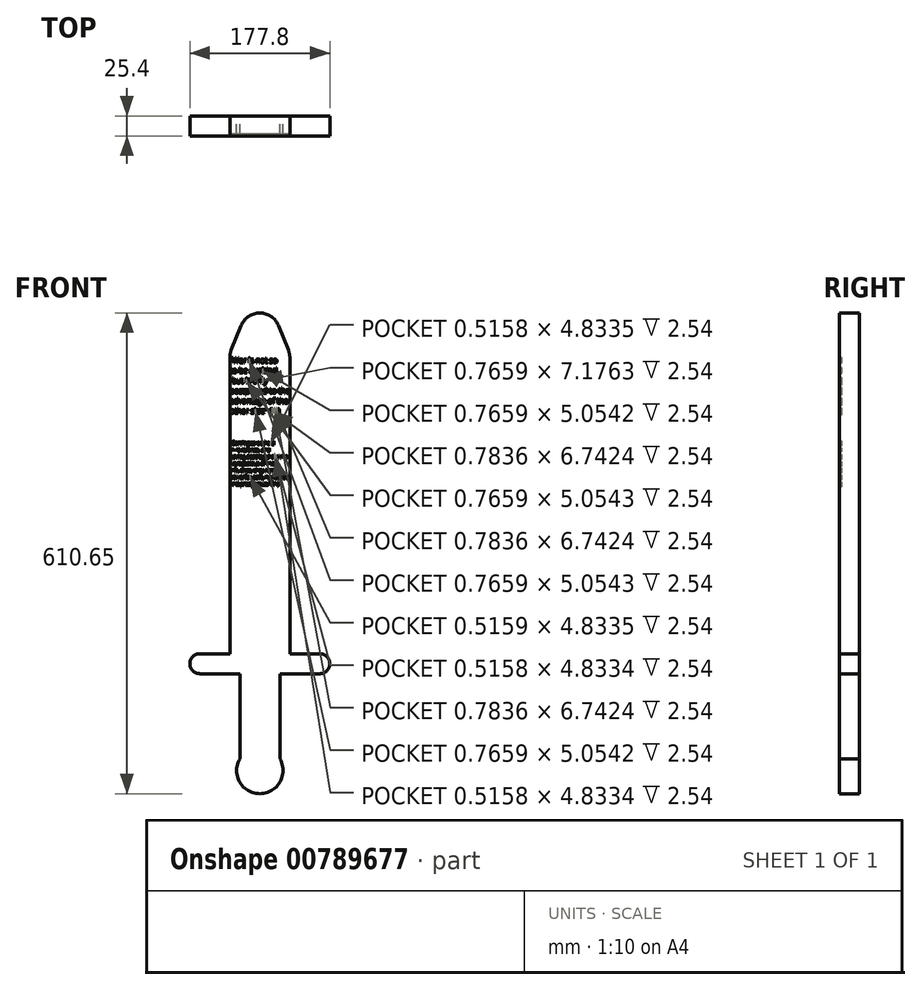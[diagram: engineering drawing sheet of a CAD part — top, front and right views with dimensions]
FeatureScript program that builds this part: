
annotation { "Feature Type Name" : "Feature", "Feature Type Description" : "" }
export const myFeature = defineFeature(function(context is Context, id is Id, definition is map)
    precondition{}
    {
        {
            var Q0;
            Q0=qCreatedBy(makeId("Front.planeOp"),FACE);
            var sketch = newSketch(context, id + "F0", { "sketchPlane" : qUnion([Q0])});
            skLineSegment(sketch, "E0", {"start": v(-25.4, -115.44) * mm, "end": v(-25.4, 36.96) * mm});
            skLineSegment(sketch, "E1", {"start": v(0, -71) * mm, "end": v(0, 36.96) * mm});
            skLineSegment(sketch, "E2", {"start": v(0, -71) * mm, "end": v(-25.4, -71) * mm, "construction": true});
            skArc(sketch, "E3", {"start": v(-25.4, -115.44) * mm, "mid": v(0.2, -100.59) * mm, "end": v(0, -71) * mm});
            skLineSegment(sketch, "E4", {"start": v(-25.4, 36.96) * mm, "end": v(0, 36.96) * mm});
            skLineSegment(sketch, "E5.MirrorCS", {"start": v(-50.8, -71) * mm, "end": v(-50.8, 36.96) * mm});
            skArc(sketch, "E6.MirrorCS", {"start": v(-25.4, -115.44) * mm, "mid": v(-51, -100.59) * mm, "end": v(-50.8, -71) * mm});
            skLineSegment(sketch, "E7.MirrorCS", {"start": v(-25.4, 36.96) * mm, "end": v(-50.8, 36.96) * mm});
            skLineSegment(sketch, "E8.bottom", {"start": v(-114.3, 36.96) * mm, "end": v(63.5, 36.96) * mm});
            skLineSegment(sketch, "E8.top", {"start": v(-114.3, 62.36) * mm, "end": v(63.5, 62.36) * mm});
            skLineSegment(sketch, "E8.left", {"start": v(-114.3, 36.96) * mm, "end": v(-114.3, 62.36) * mm});
            skLineSegment(sketch, "E8.right", {"start": v(63.5, 36.96) * mm, "end": v(63.5, 62.36) * mm});
            skLineSegment(sketch, "E9", {"start": v(-50.8, 36.96) * mm, "end": v(-50.8, 62.36) * mm, "construction": true});
            skLineSegment(sketch, "E10", {"start": v(0, 62.36) * mm, "end": v(0, 36.96) * mm, "construction": true});
            skPoint(sketch, "E11.endSnap0", {"position": v(-12.7, 36.96) * mm});
            skLineSegment(sketch, "E12", {"start": v(-25.4, 62.36) * mm, "end": v(-25.4, 36.96) * mm, "construction": true});
            skLineSegment(sketch, "E13", {"start": v(-25.4, 62.36) * mm, "end": v(-25.4, 443.36) * mm, "construction": true});
            skLineSegment(sketch, "E14", {"start": v(12.7, 62.36) * mm, "end": v(12.7, 443.36) * mm});
            skLineSegment(sketch, "E15", {"start": v(12.7, 443.36) * mm, "end": v(-63.5, 443.36) * mm});
            skLineSegment(sketch, "E16", {"start": v(-63.5, 443.36) * mm, "end": v(-63.5, 62.36) * mm});
            skLineSegment(sketch, "E17", {"start": v(-25.4, 443.36) * mm, "end": v(-25.4, 537.54) * mm, "construction": true});
            skLineSegment(sketch, "E18", {"start": v(-63.5, 443.36) * mm, "end": v(-25.4, 537.54) * mm});
            skLineSegment(sketch, "E19", {"start": v(12.7, 443.36) * mm, "end": v(-25.4, 537.54) * mm});
            skSolve(sketch);
        }
        {
            var Q0;
            {var subQ0=sQuery(id+"F0.wireOp",EDGE,"E0");Q0=makeQuery(id+"F0.imprint","IMPRINT",FACE,{"disambiguationData":[TD([[makeQuery(id+"F0.imprint","IMPRINT",EDGE,{"derivedFrom":subQ0}),1.0]])]});}
            var Q1;
            {var subQ0=sQuery(id+"F0.wireOp",EDGE,"E0");Q1=makeQuery(id+"F0.imprint","IMPRINT",FACE,{"disambiguationData":[TD([[makeQuery(id+"F0.imprint","IMPRINT",EDGE,{"derivedFrom":subQ0}),-1.0]])]});}
            var Q2;
            {var subQ5=sQuery(id+"F0.wireOp",EDGE,"E8.left");Q2=makeQuery(id+"F0.imprint","IMPRINT",FACE,{"disambiguationData":[TD([[makeQuery(id+"F0.imprint","IMPRINT",EDGE,{"derivedFrom":subQ5}),-1.0]])]});}
            var Q3;
            {var subQ0=sQuery(id+"F0.wireOp",EDGE,"k9AxdfFr-KBrS-fMyl-MdHl-o8JCi0EdSjDJ");Q3=makeQuery(id+"F0.imprint","IMPRINT",FACE,{"disambiguationData":[TD([[makeQuery(id+"F0.imprint","IMPRINT",EDGE,{"derivedFrom":subQ0}),-1.0]])]});}
            var Q4;
            {var subQ0=sQuery(id+"F0.wireOp",EDGE,"E14");Q4=makeQuery(id+"F0.imprint","IMPRINT",FACE,{"disambiguationData":[TD([[makeQuery(id+"F0.imprint","IMPRINT",EDGE,{"derivedFrom":subQ0}),1.0]])]});}
            var Q5;
            Q5=makeQuery(id+"F0.imprint","IMPRINT",FACE,{"disambiguationData":[TD([[makeQuery(id+"F0.imprint","IMPRINT",EDGE,{"derivedFrom":sQuery(id+"F0.wireOp",EDGE,"E15")}),-1.0]])]});
            var Q6;
            Q6=sQuery(id+"F0.wireOp",EDGE,"k9AxdfFr-KBrS-fMyl-MdHl-o8JCi0EdSjDJ");
            extrude(context, id + "F1", {"entities" : qUnion([Q0, Q1, Q2, Q3, Q4, Q5]), "surfaceEntities" : qUnion([Q6]), "depth" : 25.4 * mm, "offsetDistance" : 25.4 * mm});
        }
        {
            var Q0;
            Q0=makeQuery(id+"F1.opExtrude","SWEPT_EDGE",EDGE,{"disambiguationData":[OSD([sQuery(id+"F0.wireOp",EDGE,"E18"),sQuery(id+"F0.wireOp",EDGE,"E19")])]});
            var Q1;
            Q1=makeQuery(id+"F1.opExtrude","SWEPT_EDGE",EDGE,{"disambiguationData":[OSD([sQuery(id+"F0.wireOp",EDGE,"E14"),sQuery(id+"F0.wireOp",EDGE,"E15"),sQuery(id+"F0.wireOp",EDGE,"E19")])]});
            var Q2;
            Q2=makeQuery(id+"F1.opExtrude","SWEPT_EDGE",EDGE,{"disambiguationData":[OSD([sQuery(id+"F0.wireOp",EDGE,"E15"),sQuery(id+"F0.wireOp",EDGE,"E16"),sQuery(id+"F0.wireOp",EDGE,"E18")])]});
            fillet(context, id + "F2", {"entities" : qUnion([Q0, Q1, Q2]), "radius" : 25.4 * mm, "tangentPropagation" : true, "allowEdgeOverflow" : false});
        }
        {
            var Q0;
            Q0=makeQuery(id+"F1.opExtrude","SWEPT_EDGE",EDGE,{"disambiguationData":[OSD([sQuery(id+"F0.wireOp",EDGE,"E8.top"),sQuery(id+"F0.wireOp",EDGE,"E8.left")])]});
            var Q1;
            Q1=makeQuery(id+"F1.opExtrude","SWEPT_EDGE",EDGE,{"disambiguationData":[OSD([sQuery(id+"F0.wireOp",EDGE,"E8.bottom"),sQuery(id+"F0.wireOp",EDGE,"E8.left")])]});
            var Q2;
            Q2=makeQuery(id+"F1.opExtrude","SWEPT_EDGE",EDGE,{"disambiguationData":[OSD([sQuery(id+"F0.wireOp",EDGE,"E8.top"),sQuery(id+"F0.wireOp",EDGE,"E8.right")])]});
            var Q3;
            Q3=makeQuery(id+"F1.opExtrude","SWEPT_EDGE",EDGE,{"disambiguationData":[OSD([sQuery(id+"F0.wireOp",EDGE,"E8.bottom"),sQuery(id+"F0.wireOp",EDGE,"E8.right")])]});
            fillet(context, id + "F3", {"entities" : qUnion([Q0, Q1, Q2, Q3]), "radius" : 12.7 * mm, "tangentPropagation" : true, "allowEdgeOverflow" : false});
        }
        {
            var Q0;
            Q0=makeQuery(id+"F1.opExtrude","CAP_FACE",FACE,{"disambiguationData":[OSD([sQuery(id+"F0.wireOp",EDGE,"E1"),sQuery(id+"F0.wireOp",EDGE,"E3"),sQuery(id+"F0.wireOp",EDGE,"E5.MirrorCS"),sQuery(id+"F0.wireOp",EDGE,"E6.MirrorCS"),sQuery(id+"F0.wireOp",EDGE,"E8.bottom"),sQuery(id+"F0.wireOp",EDGE,"E8.top"),sQuery(id+"F0.wireOp",EDGE,"E8.left"),sQuery(id+"F0.wireOp",EDGE,"E8.right"),sQuery(id+"F0.wireOp",EDGE,"E14"),sQuery(id+"F0.wireOp",EDGE,"E16"),sQuery(id+"F0.wireOp",EDGE,"E18"),sQuery(id+"F0.wireOp",EDGE,"E19")])],"isStart":false});
            var sketch = newSketch(context, id + "F4", { "sketchPlane" : qUnion([Q0])});
            skText(sketch, "E20", { "text": "“War is not so \nto be avoided,\n but is only \npostponed to the \nadvantage of the \nother side” (III)", "fontName": "OpenSans-Regular.ttf"});
            skText(sketch, "E21", { "text": "“Coming to be held \nin reverence, and \nhaving destroyed all who \nwere jealous of their \ninfluence, they remain \npowerful, safe, honoured, \nand prosperous.” (VI)", "fontName": "OpenSans-Regular.ttf"});
            const initialGuessF4  = {"E20": [-0.0635, 0.43161, 1, 0, 0.0068], "E21": [-0.0635, 0.32779, 1, 0, 0.00458]};
            skSetInitialGuess(sketch, initialGuessF4);
            skSolve(sketch);
        }
        {
            var Q0;
            Q0=makeQuery(id+"F4.imprint","IMPRINT",FACE,{"disambiguationData":[TD([[makeQuery(id+"F4.imprint","IMPRINT",EDGE,{"derivedFrom":sQuery(id+"F4.wireOp",EDGE,"E20.sketch_text.stroke-614")}),-1.0]])]});
            var Q1;
            Q1=makeQuery(id+"F4.imprint","IMPRINT",FACE,{"disambiguationData":[TD([[makeQuery(id+"F4.imprint","IMPRINT",EDGE,{"derivedFrom":sQuery(id+"F4.wireOp",EDGE,"E20.sketch_text.stroke-363")}),1.0]])]});
            var Q2;
            Q2=makeQuery(id+"F4.imprint","IMPRINT",FACE,{"disambiguationData":[TD([[makeQuery(id+"F4.imprint","IMPRINT",EDGE,{"derivedFrom":sQuery(id+"F4.wireOp",EDGE,"E21.sketch_text.stroke-2180")}),1.0]])]});
            var Q3;
            Q3=makeQuery(id+"F4.imprint","IMPRINT",FACE,{"disambiguationData":[TD([[makeQuery(id+"F4.imprint","IMPRINT",EDGE,{"derivedFrom":sQuery(id+"F4.wireOp",EDGE,"E21.sketch_text.stroke-1878")}),1.0]])]});
            var Q4;
            Q4=makeQuery(id+"F4.imprint","IMPRINT",FACE,{"disambiguationData":[TD([[makeQuery(id+"F4.imprint","IMPRINT",EDGE,{"derivedFrom":sQuery(id+"F4.wireOp",EDGE,"E21.sketch_text.stroke-1614")}),1.0]])]});
            var Q5;
            Q5=makeQuery(id+"F4.imprint","IMPRINT",FACE,{"disambiguationData":[TD([[makeQuery(id+"F4.imprint","IMPRINT",EDGE,{"derivedFrom":sQuery(id+"F4.wireOp",EDGE,"E21.sketch_text.stroke-1142")}),1.0]])]});
            var Q6;
            Q6=makeQuery(id+"F4.imprint","IMPRINT",FACE,{"disambiguationData":[TD([[makeQuery(id+"F4.imprint","IMPRINT",EDGE,{"derivedFrom":sQuery(id+"F4.wireOp",EDGE,"E20.sketch_text.stroke-674")}),1.0]])]});
            var Q7;
            Q7=makeQuery(id+"F4.imprint","IMPRINT",FACE,{"disambiguationData":[TD([[makeQuery(id+"F4.imprint","IMPRINT",EDGE,{"derivedFrom":sQuery(id+"F4.wireOp",EDGE,"E20.sketch_text.stroke-406")}),1.0]])]});
            var Q8;
            Q8=makeQuery(id+"F4.imprint","IMPRINT",FACE,{"disambiguationData":[TD([[makeQuery(id+"F4.imprint","IMPRINT",EDGE,{"derivedFrom":sQuery(id+"F4.wireOp",EDGE,"E20.sketch_text.stroke-995")}),1.0]])]});
            var Q9;
            Q9=makeQuery(id+"F4.imprint","IMPRINT",FACE,{"disambiguationData":[TD([[makeQuery(id+"F4.imprint","IMPRINT",EDGE,{"derivedFrom":sQuery(id+"F4.wireOp",EDGE,"E20.sketch_text.stroke-692")}),1.0]])]});
            var Q10;
            Q10=makeQuery(id+"F4.imprint","IMPRINT",FACE,{"disambiguationData":[TD([[makeQuery(id+"F4.imprint","IMPRINT",EDGE,{"derivedFrom":sQuery(id+"F4.wireOp",EDGE,"E20.sketch_text.stroke-1294")}),1.0]])]});
            var Q11;
            Q11=makeQuery(id+"F4.imprint","IMPRINT",FACE,{"disambiguationData":[TD([[makeQuery(id+"F4.imprint","IMPRINT",EDGE,{"derivedFrom":sQuery(id+"F4.wireOp",EDGE,"E20.sketch_text.stroke-1032")}),1.0]])]});
            var Q12;
            Q12=makeQuery(id+"F4.imprint","IMPRINT",FACE,{"disambiguationData":[TD([[makeQuery(id+"F4.imprint","IMPRINT",EDGE,{"derivedFrom":sQuery(id+"F4.wireOp",EDGE,"E20.sketch_text.stroke-437")}),1.0]])]});
            var Q13;
            Q13=makeQuery(id+"F4.imprint","IMPRINT",FACE,{"disambiguationData":[TD([[makeQuery(id+"F4.imprint","IMPRINT",EDGE,{"derivedFrom":sQuery(id+"F4.wireOp",EDGE,"E20.sketch_text.stroke-1041")}),1.0]])]});
            var Q14;
            Q14=makeQuery(id+"F4.imprint","IMPRINT",FACE,{"disambiguationData":[TD([[makeQuery(id+"F4.imprint","IMPRINT",EDGE,{"derivedFrom":sQuery(id+"F4.wireOp",EDGE,"E21.sketch_text.stroke-925")}),1.0]])]});
            var Q15;
            Q15=makeQuery(id+"F4.imprint","IMPRINT",FACE,{"disambiguationData":[TD([[makeQuery(id+"F4.imprint","IMPRINT",EDGE,{"derivedFrom":sQuery(id+"F4.wireOp",EDGE,"E21.sketch_text.stroke-649")}),1.0]])]});
            var Q16;
            Q16=makeQuery(id+"F4.imprint","IMPRINT",FACE,{"disambiguationData":[TD([[makeQuery(id+"F4.imprint","IMPRINT",EDGE,{"derivedFrom":sQuery(id+"F4.wireOp",EDGE,"E21.sketch_text.stroke-1950")}),1.0]])]});
            var Q17;
            Q17=makeQuery(id+"F4.imprint","IMPRINT",FACE,{"disambiguationData":[TD([[makeQuery(id+"F4.imprint","IMPRINT",EDGE,{"derivedFrom":sQuery(id+"F4.wireOp",EDGE,"E20.sketch_text.stroke-731")}),1.0]])]});
            var Q18;
            Q18=makeQuery(id+"F4.imprint","IMPRINT",FACE,{"disambiguationData":[TD([[makeQuery(id+"F4.imprint","IMPRINT",EDGE,{"derivedFrom":sQuery(id+"F4.wireOp",EDGE,"E21.sketch_text.stroke-139")}),1.0]])]});
            var Q19;
            Q19=makeQuery(id+"F4.imprint","IMPRINT",FACE,{"disambiguationData":[TD([[makeQuery(id+"F4.imprint","IMPRINT",EDGE,{"derivedFrom":sQuery(id+"F4.wireOp",EDGE,"E20.sketch_text.stroke-422")}),-1.0]])]});
            var Q20;
            Q20=makeQuery(id+"F4.imprint","IMPRINT",FACE,{"disambiguationData":[TD([[makeQuery(id+"F4.imprint","IMPRINT",EDGE,{"derivedFrom":sQuery(id+"F4.wireOp",EDGE,"E20.sketch_text.stroke-751")}),1.0]])]});
            var Q21;
            Q21=makeQuery(id+"F4.imprint","IMPRINT",FACE,{"disambiguationData":[TD([[makeQuery(id+"F4.imprint","IMPRINT",EDGE,{"derivedFrom":sQuery(id+"F4.wireOp",EDGE,"E20.sketch_text.stroke-1075")}),1.0]])]});
            var Q22;
            Q22=makeQuery(id+"F4.imprint","IMPRINT",FACE,{"disambiguationData":[TD([[makeQuery(id+"F4.imprint","IMPRINT",EDGE,{"derivedFrom":sQuery(id+"F4.wireOp",EDGE,"E21.sketch_text.stroke-679")}),1.0]])]});
            var Q23;
            Q23=makeQuery(id+"F4.imprint","IMPRINT",FACE,{"disambiguationData":[TD([[makeQuery(id+"F4.imprint","IMPRINT",EDGE,{"derivedFrom":sQuery(id+"F4.wireOp",EDGE,"E20.sketch_text.stroke-518")}),-1.0]])]});
            var Q24;
            Q24=makeQuery(id+"F4.imprint","IMPRINT",FACE,{"disambiguationData":[TD([[makeQuery(id+"F4.imprint","IMPRINT",EDGE,{"derivedFrom":sQuery(id+"F4.wireOp",EDGE,"E20.sketch_text.stroke-1156")}),-1.0]])]});
            var Q25;
            Q25=makeQuery(id+"F4.imprint","IMPRINT",FACE,{"disambiguationData":[TD([[makeQuery(id+"F4.imprint","IMPRINT",EDGE,{"derivedFrom":sQuery(id+"F4.wireOp",EDGE,"E20.sketch_text.stroke-255")}),1.0]])]});
            var Q26;
            Q26=makeQuery(id+"F4.imprint","IMPRINT",FACE,{"disambiguationData":[TD([[makeQuery(id+"F4.imprint","IMPRINT",EDGE,{"derivedFrom":sQuery(id+"F4.wireOp",EDGE,"E20.sketch_text.stroke-232")}),1.0]])]});
            var Q27;
            Q27=makeQuery(id+"F4.imprint","IMPRINT",FACE,{"disambiguationData":[TD([[makeQuery(id+"F4.imprint","IMPRINT",EDGE,{"derivedFrom":sQuery(id+"F4.wireOp",EDGE,"E20.sketch_text.stroke-51")}),1.0]])]});
            var Q28;
            Q28=makeQuery(id+"F4.imprint","IMPRINT",FACE,{"disambiguationData":[TD([[makeQuery(id+"F4.imprint","IMPRINT",EDGE,{"derivedFrom":sQuery(id+"F4.wireOp",EDGE,"E20.sketch_text.stroke-135")}),1.0]])]});
            var Q29;
            Q29=makeQuery(id+"F4.imprint","IMPRINT",FACE,{"disambiguationData":[TD([[makeQuery(id+"F4.imprint","IMPRINT",EDGE,{"derivedFrom":sQuery(id+"F4.wireOp",EDGE,"E20.sketch_text.stroke-196")}),1.0]])]});
            var Q30;
            Q30=makeQuery(id+"F4.imprint","IMPRINT",FACE,{"disambiguationData":[TD([[makeQuery(id+"F4.imprint","IMPRINT",EDGE,{"derivedFrom":sQuery(id+"F4.wireOp",EDGE,"E21.sketch_text.stroke-2050")}),1.0]])]});
            var Q31;
            Q31=makeQuery(id+"F4.imprint","IMPRINT",FACE,{"disambiguationData":[TD([[makeQuery(id+"F4.imprint","IMPRINT",EDGE,{"derivedFrom":sQuery(id+"F4.wireOp",EDGE,"E21.sketch_text.stroke-173")}),1.0]])]});
            var Q32;
            Q32=makeQuery(id+"F4.imprint","IMPRINT",FACE,{"disambiguationData":[TD([[makeQuery(id+"F4.imprint","IMPRINT",EDGE,{"derivedFrom":sQuery(id+"F4.wireOp",EDGE,"E20.sketch_text.stroke-1335")}),-1.0]])]});
            var Q33;
            Q33=makeQuery(id+"F4.imprint","IMPRINT",FACE,{"disambiguationData":[TD([[makeQuery(id+"F4.imprint","IMPRINT",EDGE,{"derivedFrom":sQuery(id+"F4.wireOp",EDGE,"E20.sketch_text.stroke-788")}),1.0]])]});
            var Q34;
            Q34=makeQuery(id+"F4.imprint","IMPRINT",FACE,{"disambiguationData":[TD([[makeQuery(id+"F4.imprint","IMPRINT",EDGE,{"derivedFrom":sQuery(id+"F4.wireOp",EDGE,"E21.sketch_text.stroke-196")}),1.0]])]});
            var Q35;
            Q35=makeQuery(id+"F4.imprint","IMPRINT",FACE,{"disambiguationData":[TD([[makeQuery(id+"F4.imprint","IMPRINT",EDGE,{"derivedFrom":sQuery(id+"F4.wireOp",EDGE,"E21.sketch_text.stroke-2025")}),1.0]])]});
            var Q36;
            Q36=makeQuery(id+"F4.imprint","IMPRINT",FACE,{"disambiguationData":[TD([[makeQuery(id+"F4.imprint","IMPRINT",EDGE,{"derivedFrom":sQuery(id+"F4.wireOp",EDGE,"E20.sketch_text.stroke-527")}),1.0]])]});
            var Q37;
            Q37=makeQuery(id+"F4.imprint","IMPRINT",FACE,{"disambiguationData":[TD([[makeQuery(id+"F4.imprint","IMPRINT",EDGE,{"derivedFrom":sQuery(id+"F4.wireOp",EDGE,"E20.sketch_text.stroke-1165")}),1.0]])]});
            var Q38;
            Q38=makeQuery(id+"F4.imprint","IMPRINT",FACE,{"disambiguationData":[TD([[makeQuery(id+"F4.imprint","IMPRINT",EDGE,{"derivedFrom":sQuery(id+"F4.wireOp",EDGE,"E20.sketch_text.stroke-847")}),1.0]])]});
            var Q39;
            Q39=makeQuery(id+"F4.imprint","IMPRINT",FACE,{"disambiguationData":[TD([[makeQuery(id+"F4.imprint","IMPRINT",EDGE,{"derivedFrom":sQuery(id+"F4.wireOp",EDGE,"E20.sketch_text.stroke-301")}),1.0]])]});
            var Q40;
            Q40=makeQuery(id+"F4.imprint","IMPRINT",FACE,{"disambiguationData":[TD([[makeQuery(id+"F4.imprint","IMPRINT",EDGE,{"derivedFrom":sQuery(id+"F4.wireOp",EDGE,"E21.sketch_text.stroke-773")}),1.0]])]});
            var Q41;
            Q41=makeQuery(id+"F4.imprint","IMPRINT",FACE,{"disambiguationData":[TD([[makeQuery(id+"F4.imprint","IMPRINT",EDGE,{"derivedFrom":sQuery(id+"F4.wireOp",EDGE,"E21.sketch_text.stroke-2081")}),1.0]])]});
            var Q42;
            Q42=makeQuery(id+"F4.imprint","IMPRINT",FACE,{"disambiguationData":[TD([[makeQuery(id+"F4.imprint","IMPRINT",EDGE,{"derivedFrom":sQuery(id+"F4.wireOp",EDGE,"E20.sketch_text.stroke-871")}),1.0]])]});
            var Q43;
            Q43=makeQuery(id+"F4.imprint","IMPRINT",FACE,{"disambiguationData":[TD([[makeQuery(id+"F4.imprint","IMPRINT",EDGE,{"derivedFrom":sQuery(id+"F4.wireOp",EDGE,"E21.sketch_text.stroke-1062")}),1.0]])]});
            var Q44;
            Q44=makeQuery(id+"F4.imprint","IMPRINT",FACE,{"disambiguationData":[TD([[makeQuery(id+"F4.imprint","IMPRINT",EDGE,{"derivedFrom":sQuery(id+"F4.wireOp",EDGE,"E20.sketch_text.stroke-1192")}),-1.0]])]});
            var Q45;
            Q45=makeQuery(id+"F4.imprint","IMPRINT",FACE,{"disambiguationData":[TD([[makeQuery(id+"F4.imprint","IMPRINT",EDGE,{"derivedFrom":sQuery(id+"F4.wireOp",EDGE,"E20.sketch_text.stroke-894")}),1.0]])]});
            var Q46;
            Q46=makeQuery(id+"F4.imprint","IMPRINT",FACE,{"disambiguationData":[TD([[makeQuery(id+"F4.imprint","IMPRINT",EDGE,{"derivedFrom":sQuery(id+"F4.wireOp",EDGE,"E20.sketch_text.stroke-328")}),1.0]])]});
            var Q47;
            Q47=makeQuery(id+"F4.imprint","IMPRINT",FACE,{"disambiguationData":[TD([[makeQuery(id+"F4.imprint","IMPRINT",EDGE,{"derivedFrom":sQuery(id+"F4.wireOp",EDGE,"E21.sketch_text.stroke-527")}),1.0]])]});
            var Q48;
            Q48=makeQuery(id+"F4.imprint","IMPRINT",FACE,{"disambiguationData":[TD([[makeQuery(id+"F4.imprint","IMPRINT",EDGE,{"derivedFrom":sQuery(id+"F4.wireOp",EDGE,"E21.sketch_text.stroke-279")}),1.0]])]});
            var Q49;
            Q49=makeQuery(id+"F4.imprint","IMPRINT",FACE,{"disambiguationData":[TD([[makeQuery(id+"F4.imprint","IMPRINT",EDGE,{"derivedFrom":sQuery(id+"F4.wireOp",EDGE,"E21.sketch_text.stroke-2130")}),1.0]])]});
            var Q50;
            Q50=makeQuery(id+"F4.imprint","IMPRINT",FACE,{"disambiguationData":[TD([[makeQuery(id+"F4.imprint","IMPRINT",EDGE,{"derivedFrom":sQuery(id+"F4.wireOp",EDGE,"E20.sketch_text.stroke-1224")}),1.0]])]});
            var Q51;
            Q51=makeQuery(id+"F4.imprint","IMPRINT",FACE,{"disambiguationData":[TD([[makeQuery(id+"F4.imprint","IMPRINT",EDGE,{"derivedFrom":sQuery(id+"F4.wireOp",EDGE,"E20.sketch_text.stroke-588")}),1.0]])]});
            var Q52;
            Q52=makeQuery(id+"F4.imprint","IMPRINT",FACE,{"disambiguationData":[TD([[makeQuery(id+"F4.imprint","IMPRINT",EDGE,{"derivedFrom":sQuery(id+"F4.wireOp",EDGE,"E21.sketch_text.stroke-831")}),1.0]])]});
            var Q53;
            Q53=makeQuery(id+"F4.imprint","IMPRINT",FACE,{"disambiguationData":[TD([[makeQuery(id+"F4.imprint","IMPRINT",EDGE,{"derivedFrom":sQuery(id+"F4.wireOp",EDGE,"E21.sketch_text.stroke-1844")}),1.0]])]});
            var Q54;
            Q54=makeQuery(id+"F4.imprint","IMPRINT",FACE,{"disambiguationData":[TD([[makeQuery(id+"F4.imprint","IMPRINT",EDGE,{"derivedFrom":sQuery(id+"F4.wireOp",EDGE,"E21.sketch_text.stroke-1083")}),1.0]])]});
            var Q55;
            Q55=makeQuery(id+"F4.imprint","IMPRINT",FACE,{"disambiguationData":[TD([[makeQuery(id+"F4.imprint","IMPRINT",EDGE,{"derivedFrom":sQuery(id+"F4.wireOp",EDGE,"E20.sketch_text.stroke-932")}),1.0]])]});
            var Q56;
            Q56=makeQuery(id+"F4.imprint","IMPRINT",FACE,{"disambiguationData":[TD([[makeQuery(id+"F4.imprint","IMPRINT",EDGE,{"derivedFrom":sQuery(id+"F4.wireOp",EDGE,"E20.sketch_text.stroke-606")}),1.0]])]});
            var Q57;
            Q57=makeQuery(id+"F4.imprint","IMPRINT",FACE,{"disambiguationData":[TD([[makeQuery(id+"F4.imprint","IMPRINT",EDGE,{"derivedFrom":sQuery(id+"F4.wireOp",EDGE,"E21.sketch_text.stroke-36")}),1.0]])]});
            var Q58;
            Q58=makeQuery(id+"F4.imprint","IMPRINT",FACE,{"disambiguationData":[TD([[makeQuery(id+"F4.imprint","IMPRINT",EDGE,{"derivedFrom":sQuery(id+"F4.wireOp",EDGE,"E21.sketch_text.stroke-1596")}),1.0]])]});
            var Q59;
            Q59=makeQuery(id+"F4.imprint","IMPRINT",FACE,{"disambiguationData":[TD([[makeQuery(id+"F4.imprint","IMPRINT",EDGE,{"derivedFrom":sQuery(id+"F4.wireOp",EDGE,"E21.sketch_text.stroke-300")}),-1.0]])]});
            var Q60;
            Q60=makeQuery(id+"F4.imprint","IMPRINT",FACE,{"disambiguationData":[TD([[makeQuery(id+"F4.imprint","IMPRINT",EDGE,{"derivedFrom":sQuery(id+"F4.wireOp",EDGE,"E21.sketch_text.stroke-44")}),-1.0]])]});
            var Q61;
            Q61=makeQuery(id+"F4.imprint","IMPRINT",FACE,{"disambiguationData":[TD([[makeQuery(id+"F4.imprint","IMPRINT",EDGE,{"derivedFrom":sQuery(id+"F4.wireOp",EDGE,"E20.sketch_text.stroke-1242")}),-1.0]])]});
            var Q62;
            Q62=makeQuery(id+"F4.imprint","IMPRINT",FACE,{"disambiguationData":[TD([[makeQuery(id+"F4.imprint","IMPRINT",EDGE,{"derivedFrom":sQuery(id+"F4.wireOp",EDGE,"E20.sketch_text.stroke-940")}),-1.0]])]});
            var Q63;
            Q63=makeQuery(id+"F4.imprint","IMPRINT",FACE,{"disambiguationData":[TD([[makeQuery(id+"F4.imprint","IMPRINT",EDGE,{"derivedFrom":sQuery(id+"F4.wireOp",EDGE,"E21.sketch_text.stroke-1334")}),-1.0]])]});
            var Q64;
            Q64=makeQuery(id+"F4.imprint","IMPRINT",FACE,{"disambiguationData":[TD([[makeQuery(id+"F4.imprint","IMPRINT",EDGE,{"derivedFrom":sQuery(id+"F4.wireOp",EDGE,"E21.sketch_text.stroke-1108")}),-1.0]])]});
            var Q65;
            Q65=makeQuery(id+"F4.imprint","IMPRINT",FACE,{"disambiguationData":[TD([[makeQuery(id+"F4.imprint","IMPRINT",EDGE,{"derivedFrom":sQuery(id+"F4.wireOp",EDGE,"E21.sketch_text.stroke-867")}),-1.0]])]});
            var Q66;
            Q66=makeQuery(id+"F4.imprint","IMPRINT",FACE,{"disambiguationData":[TD([[makeQuery(id+"F4.imprint","IMPRINT",EDGE,{"derivedFrom":sQuery(id+"F4.wireOp",EDGE,"E21.sketch_text.stroke-581")}),-1.0]])]});
            var Q67;
            Q67=makeQuery(id+"F4.imprint","IMPRINT",FACE,{"disambiguationData":[TD([[makeQuery(id+"F4.imprint","IMPRINT",EDGE,{"derivedFrom":sQuery(id+"F4.wireOp",EDGE,"E20.sketch_text.stroke-282")}),-1.0]])]});
            var Q68;
            Q68=makeQuery(id+"F4.imprint","IMPRINT",FACE,{"disambiguationData":[TD([[makeQuery(id+"F4.imprint","IMPRINT",EDGE,{"derivedFrom":sQuery(id+"F4.wireOp",EDGE,"E21.sketch_text.stroke-1869")}),-1.0]])]});
            var Q69;
            Q69=makeQuery(id+"F4.imprint","IMPRINT",FACE,{"disambiguationData":[TD([[makeQuery(id+"F4.imprint","IMPRINT",EDGE,{"derivedFrom":sQuery(id+"F4.wireOp",EDGE,"E21.sketch_text.stroke-1024")}),-1.0]])]});
            var Q70;
            Q70=makeQuery(id+"F4.imprint","IMPRINT",FACE,{"disambiguationData":[TD([[makeQuery(id+"F4.imprint","IMPRINT",EDGE,{"derivedFrom":sQuery(id+"F4.wireOp",EDGE,"E21.sketch_text.stroke-330")}),-1.0]])]});
            var Q71;
            Q71=makeQuery(id+"F4.imprint","IMPRINT",FACE,{"disambiguationData":[TD([[makeQuery(id+"F4.imprint","IMPRINT",EDGE,{"derivedFrom":sQuery(id+"F4.wireOp",EDGE,"E20.sketch_text.stroke-879")}),-1.0]])]});
            var Q72;
            Q72=makeQuery(id+"F4.imprint","IMPRINT",FACE,{"disambiguationData":[TD([[makeQuery(id+"F4.imprint","IMPRINT",EDGE,{"derivedFrom":sQuery(id+"F4.wireOp",EDGE,"E20.sketch_text.stroke-1267")}),-1.0]])]});
            var Q73;
            Q73=makeQuery(id+"F4.imprint","IMPRINT",FACE,{"disambiguationData":[TD([[makeQuery(id+"F4.imprint","IMPRINT",EDGE,{"derivedFrom":sQuery(id+"F4.wireOp",EDGE,"E20.sketch_text.stroke-957")}),-1.0]])]});
            var Q74;
            Q74=makeQuery(id+"F4.imprint","IMPRINT",FACE,{"disambiguationData":[TD([[makeQuery(id+"F4.imprint","IMPRINT",EDGE,{"derivedFrom":sQuery(id+"F4.wireOp",EDGE,"E21.sketch_text.stroke-1351")}),-1.0]])]});
            var Q75;
            Q75=makeQuery(id+"F4.imprint","IMPRINT",FACE,{"disambiguationData":[TD([[makeQuery(id+"F4.imprint","IMPRINT",EDGE,{"derivedFrom":sQuery(id+"F4.wireOp",EDGE,"E21.sketch_text.stroke-871")}),-1.0]])]});
            var Q76;
            Q76=makeQuery(id+"F4.imprint","IMPRINT",FACE,{"disambiguationData":[TD([[makeQuery(id+"F4.imprint","IMPRINT",EDGE,{"derivedFrom":sQuery(id+"F4.wireOp",EDGE,"E21.sketch_text.stroke-591")}),-1.0]])]});
            var Q77;
            Q77=makeQuery(id+"F4.imprint","IMPRINT",FACE,{"disambiguationData":[TD([[makeQuery(id+"F4.imprint","IMPRINT",EDGE,{"derivedFrom":sQuery(id+"F4.wireOp",EDGE,"E20.sketch_text.stroke-319")}),-1.0]])]});
            var Q78;
            Q78=makeQuery(id+"F4.imprint","IMPRINT",FACE,{"disambiguationData":[TD([[makeQuery(id+"F4.imprint","IMPRINT",EDGE,{"derivedFrom":sQuery(id+"F4.wireOp",EDGE,"E21.sketch_text.stroke-2188")}),-1.0]])]});
            var Q79;
            Q79=makeQuery(id+"F4.imprint","IMPRINT",FACE,{"disambiguationData":[TD([[makeQuery(id+"F4.imprint","IMPRINT",EDGE,{"derivedFrom":sQuery(id+"F4.wireOp",EDGE,"E21.sketch_text.stroke-1886")}),-1.0]])]});
            var Q80;
            Q80=makeQuery(id+"F4.imprint","IMPRINT",FACE,{"disambiguationData":[TD([[makeQuery(id+"F4.imprint","IMPRINT",EDGE,{"derivedFrom":sQuery(id+"F4.wireOp",EDGE,"E21.sketch_text.stroke-1622")}),-1.0]])]});
            var Q81;
            Q81=makeQuery(id+"F4.imprint","IMPRINT",FACE,{"disambiguationData":[TD([[makeQuery(id+"F4.imprint","IMPRINT",EDGE,{"derivedFrom":sQuery(id+"F4.wireOp",EDGE,"E21.sketch_text.stroke-1916")}),-1.0]])]});
            var Q82;
            Q82=makeQuery(id+"F4.imprint","IMPRINT",FACE,{"disambiguationData":[TD([[makeQuery(id+"F4.imprint","IMPRINT",EDGE,{"derivedFrom":sQuery(id+"F4.wireOp",EDGE,"E21.sketch_text.stroke-1043")}),-1.0]])]});
            var Q83;
            Q83=makeQuery(id+"F4.imprint","IMPRINT",FACE,{"disambiguationData":[TD([[makeQuery(id+"F4.imprint","IMPRINT",EDGE,{"derivedFrom":sQuery(id+"F4.wireOp",EDGE,"E21.sketch_text.stroke-359")}),-1.0]])]});
            var Q84;
            Q84=makeQuery(id+"F4.imprint","IMPRINT",FACE,{"disambiguationData":[TD([[makeQuery(id+"F4.imprint","IMPRINT",EDGE,{"derivedFrom":sQuery(id+"F4.wireOp",EDGE,"E20.sketch_text.stroke-913")}),-1.0]])]});
            var Q85;
            Q85=makeQuery(id+"F4.imprint","IMPRINT",FACE,{"disambiguationData":[TD([[makeQuery(id+"F4.imprint","IMPRINT",EDGE,{"derivedFrom":sQuery(id+"F4.wireOp",EDGE,"E20.sketch_text.stroke-639")}),-1.0]])]});
            var Q86;
            Q86=makeQuery(id+"F4.imprint","IMPRINT",FACE,{"disambiguationData":[TD([[makeQuery(id+"F4.imprint","IMPRINT",EDGE,{"derivedFrom":sQuery(id+"F4.wireOp",EDGE,"E20.sketch_text.stroke-386")}),1.0]])]});
            var Q87;
            Q87=makeQuery(id+"F4.imprint","IMPRINT",FACE,{"disambiguationData":[TD([[makeQuery(id+"F4.imprint","IMPRINT",EDGE,{"derivedFrom":sQuery(id+"F4.wireOp",EDGE,"E21.sketch_text.stroke-1150")}),-1.0]])]});
            var Q88;
            Q88=makeQuery(id+"F4.imprint","IMPRINT",FACE,{"disambiguationData":[TD([[makeQuery(id+"F4.imprint","IMPRINT",EDGE,{"derivedFrom":sQuery(id+"F4.wireOp",EDGE,"E21.sketch_text.stroke-875")}),-1.0]])]});
            var Q89;
            Q89=makeQuery(id+"F4.imprint","IMPRINT",FACE,{"disambiguationData":[TD([[makeQuery(id+"F4.imprint","IMPRINT",EDGE,{"derivedFrom":sQuery(id+"F4.wireOp",EDGE,"E20.sketch_text.stroke-348")}),-1.0]])]});
            var Q90;
            Q90=makeQuery(id+"F4.imprint","IMPRINT",FACE,{"disambiguationData":[TD([[makeQuery(id+"F4.imprint","IMPRINT",EDGE,{"derivedFrom":sQuery(id+"F4.wireOp",EDGE,"E21.sketch_text.stroke-2205")}),-1.0]])]});
            var Q91;
            Q91=makeQuery(id+"F4.imprint","IMPRINT",FACE,{"disambiguationData":[TD([[makeQuery(id+"F4.imprint","IMPRINT",EDGE,{"derivedFrom":sQuery(id+"F4.wireOp",EDGE,"E21.sketch_text.stroke-1935")}),-1.0]])]});
            var Q92;
            Q92=makeQuery(id+"F4.imprint","IMPRINT",FACE,{"disambiguationData":[TD([[makeQuery(id+"F4.imprint","IMPRINT",EDGE,{"derivedFrom":sQuery(id+"F4.wireOp",EDGE,"E21.sketch_text.stroke-1074")}),-1.0]])]});
            var Q93;
            Q93=makeQuery(id+"F4.imprint","IMPRINT",FACE,{"disambiguationData":[TD([[makeQuery(id+"F4.imprint","IMPRINT",EDGE,{"derivedFrom":sQuery(id+"F4.wireOp",EDGE,"E21.sketch_text.stroke-391")}),-1.0]])]});
            var Q94;
            Q94=makeQuery(id+"F4.imprint","IMPRINT",FACE,{"disambiguationData":[TD([[makeQuery(id+"F4.imprint","IMPRINT",EDGE,{"derivedFrom":sQuery(id+"F4.wireOp",EDGE,"E20.sketch_text.stroke-976")}),-1.0]])]});
            var Q95;
            Q95=makeQuery(id+"F4.imprint","IMPRINT",FACE,{"disambiguationData":[TD([[makeQuery(id+"F4.imprint","IMPRINT",EDGE,{"derivedFrom":sQuery(id+"F4.wireOp",EDGE,"E20.sketch_text.stroke-372")}),-1.0]])]});
            var Q96;
            Q96=makeQuery(id+"F4.imprint","IMPRINT",FACE,{"disambiguationData":[TD([[makeQuery(id+"F4.imprint","IMPRINT",EDGE,{"derivedFrom":sQuery(id+"F4.wireOp",EDGE,"E21.sketch_text.stroke-1966")}),-1.0]])]});
            var Q97;
            Q97=makeQuery(id+"F4.imprint","IMPRINT",FACE,{"disambiguationData":[TD([[makeQuery(id+"F4.imprint","IMPRINT",EDGE,{"derivedFrom":sQuery(id+"F4.wireOp",EDGE,"E21.sketch_text.stroke-1133")}),-1.0]])]});
            var Q98;
            Q98=makeQuery(id+"F4.imprint","IMPRINT",FACE,{"disambiguationData":[TD([[makeQuery(id+"F4.imprint","IMPRINT",EDGE,{"derivedFrom":sQuery(id+"F4.wireOp",EDGE,"E21.sketch_text.stroke-442")}),-1.0]])]});
            var Q99;
            Q99=makeQuery(id+"F4.imprint","IMPRINT",FACE,{"disambiguationData":[TD([[makeQuery(id+"F4.imprint","IMPRINT",EDGE,{"derivedFrom":sQuery(id+"F4.wireOp",EDGE,"E20.sketch_text.stroke-1047")}),-1.0]])]});
            var Q100;
            Q100=makeQuery(id+"F4.imprint","IMPRINT",FACE,{"disambiguationData":[TD([[makeQuery(id+"F4.imprint","IMPRINT",EDGE,{"derivedFrom":sQuery(id+"F4.wireOp",EDGE,"E20.sketch_text.stroke-415")}),-1.0]])]});
            var Q101;
            Q101=makeQuery(id+"F4.imprint","IMPRINT",FACE,{"disambiguationData":[TD([[makeQuery(id+"F4.imprint","IMPRINT",EDGE,{"derivedFrom":sQuery(id+"F4.wireOp",EDGE,"E21.sketch_text.stroke-349")}),-1.0]])]});
            var Q102;
            Q102=makeQuery(id+"F4.imprint","IMPRINT",FACE,{"disambiguationData":[TD([[makeQuery(id+"F4.imprint","IMPRINT",EDGE,{"derivedFrom":sQuery(id+"F4.wireOp",EDGE,"E21.sketch_text.stroke-84")}),-1.0]])]});
            var Q103;
            Q103=makeQuery(id+"F4.imprint","IMPRINT",FACE,{"disambiguationData":[TD([[makeQuery(id+"F4.imprint","IMPRINT",EDGE,{"derivedFrom":sQuery(id+"F4.wireOp",EDGE,"E21.sketch_text.stroke-1385")}),-1.0]])]});
            var Q104;
            Q104=makeQuery(id+"F4.imprint","IMPRINT",FACE,{"disambiguationData":[TD([[makeQuery(id+"F4.imprint","IMPRINT",EDGE,{"derivedFrom":sQuery(id+"F4.wireOp",EDGE,"E21.sketch_text.stroke-1167")}),-1.0]])]});
            var Q105;
            Q105=makeQuery(id+"F4.imprint","IMPRINT",FACE,{"disambiguationData":[TD([[makeQuery(id+"F4.imprint","IMPRINT",EDGE,{"derivedFrom":sQuery(id+"F4.wireOp",EDGE,"E21.sketch_text.stroke-898")}),-1.0]])]});
            var Q106;
            Q106=makeQuery(id+"F4.imprint","IMPRINT",FACE,{"disambiguationData":[TD([[makeQuery(id+"F4.imprint","IMPRINT",EDGE,{"derivedFrom":sQuery(id+"F4.wireOp",EDGE,"E21.sketch_text.stroke-603")}),-1.0]])]});
            var Q107;
            Q107=makeQuery(id+"F4.imprint","IMPRINT",FACE,{"disambiguationData":[TD([[makeQuery(id+"F4.imprint","IMPRINT",EDGE,{"derivedFrom":sQuery(id+"F4.wireOp",EDGE,"E21.sketch_text.stroke-2010")}),-1.0]])]});
            var Q108;
            Q108=makeQuery(id+"F4.imprint","IMPRINT",FACE,{"disambiguationData":[TD([[makeQuery(id+"F4.imprint","IMPRINT",EDGE,{"derivedFrom":sQuery(id+"F4.wireOp",EDGE,"E21.sketch_text.stroke-1204")}),-1.0]])]});
            var Q109;
            Q109=makeQuery(id+"F4.imprint","IMPRINT",FACE,{"disambiguationData":[TD([[makeQuery(id+"F4.imprint","IMPRINT",EDGE,{"derivedFrom":sQuery(id+"F4.wireOp",EDGE,"E21.sketch_text.stroke-468")}),-1.0]])]});
            var Q110;
            Q110=makeQuery(id+"F4.imprint","IMPRINT",FACE,{"disambiguationData":[TD([[makeQuery(id+"F4.imprint","IMPRINT",EDGE,{"derivedFrom":sQuery(id+"F4.wireOp",EDGE,"E20.sketch_text.stroke-1066")}),-1.0]])]});
            var Q111;
            Q111=makeQuery(id+"F4.imprint","IMPRINT",FACE,{"disambiguationData":[TD([[makeQuery(id+"F4.imprint","IMPRINT",EDGE,{"derivedFrom":sQuery(id+"F4.wireOp",EDGE,"E20.sketch_text.stroke-700")}),-1.0]])]});
            var Q112;
            Q112=makeQuery(id+"F4.imprint","IMPRINT",FACE,{"disambiguationData":[TD([[makeQuery(id+"F4.imprint","IMPRINT",EDGE,{"derivedFrom":sQuery(id+"F4.wireOp",EDGE,"E20.sketch_text.stroke-1317")}),1.0]])]});
            var Q113;
            Q113=makeQuery(id+"F4.imprint","IMPRINT",FACE,{"disambiguationData":[TD([[makeQuery(id+"F4.imprint","IMPRINT",EDGE,{"derivedFrom":sQuery(id+"F4.wireOp",EDGE,"E21.sketch_text.stroke-1392")}),-1.0]])]});
            var Q114;
            Q114=makeQuery(id+"F4.imprint","IMPRINT",FACE,{"disambiguationData":[TD([[makeQuery(id+"F4.imprint","IMPRINT",EDGE,{"derivedFrom":sQuery(id+"F4.wireOp",EDGE,"E21.sketch_text.stroke-1186")}),-1.0]])]});
            var Q115;
            Q115=makeQuery(id+"F4.imprint","IMPRINT",FACE,{"disambiguationData":[TD([[makeQuery(id+"F4.imprint","IMPRINT",EDGE,{"derivedFrom":sQuery(id+"F4.wireOp",EDGE,"E20.sketch_text.stroke-391")}),-1.0]])]});
            var Q116;
            Q116=makeQuery(id+"F4.imprint","IMPRINT",FACE,{"disambiguationData":[TD([[makeQuery(id+"F4.imprint","IMPRINT",EDGE,{"derivedFrom":sQuery(id+"F4.wireOp",EDGE,"E21.sketch_text.stroke-1677")}),-1.0]])]});
            var Q117;
            Q117=makeQuery(id+"F4.imprint","IMPRINT",FACE,{"disambiguationData":[TD([[makeQuery(id+"F4.imprint","IMPRINT",EDGE,{"derivedFrom":sQuery(id+"F4.wireOp",EDGE,"E20.sketch_text.stroke-445")}),-1.0]])]});
            var Q118;
            Q118=makeQuery(id+"F4.imprint","IMPRINT",FACE,{"disambiguationData":[TD([[makeQuery(id+"F4.imprint","IMPRINT",EDGE,{"derivedFrom":sQuery(id+"F4.wireOp",EDGE,"E21.sketch_text.stroke-378")}),-1.0]])]});
            var Q119;
            Q119=makeQuery(id+"F4.imprint","IMPRINT",FACE,{"disambiguationData":[TD([[makeQuery(id+"F4.imprint","IMPRINT",EDGE,{"derivedFrom":sQuery(id+"F4.wireOp",EDGE,"E20.sketch_text.stroke-1322")}),-1.0]])]});
            var Q120;
            Q120=makeQuery(id+"F4.imprint","IMPRINT",FACE,{"disambiguationData":[TD([[makeQuery(id+"F4.imprint","IMPRINT",EDGE,{"derivedFrom":sQuery(id+"F4.wireOp",EDGE,"E21.sketch_text.stroke-1411")}),-1.0]])]});
            var Q121;
            Q121=makeQuery(id+"F4.imprint","IMPRINT",FACE,{"disambiguationData":[TD([[makeQuery(id+"F4.imprint","IMPRINT",EDGE,{"derivedFrom":sQuery(id+"F4.wireOp",EDGE,"E21.sketch_text.stroke-933")}),-1.0]])]});
            var Q122;
            Q122=makeQuery(id+"F4.imprint","IMPRINT",FACE,{"disambiguationData":[TD([[makeQuery(id+"F4.imprint","IMPRINT",EDGE,{"derivedFrom":sQuery(id+"F4.wireOp",EDGE,"E21.sketch_text.stroke-1694")}),-1.0]])]});
            var Q123;
            Q123=makeQuery(id+"F4.imprint","IMPRINT",FACE,{"disambiguationData":[TD([[makeQuery(id+"F4.imprint","IMPRINT",EDGE,{"derivedFrom":sQuery(id+"F4.wireOp",EDGE,"E21.sketch_text.stroke-2034")}),-1.0]])]});
            var Q124;
            Q124=makeQuery(id+"F4.imprint","IMPRINT",FACE,{"disambiguationData":[TD([[makeQuery(id+"F4.imprint","IMPRINT",EDGE,{"derivedFrom":sQuery(id+"F4.wireOp",EDGE,"E21.sketch_text.stroke-1315")}),-1.0]])]});
            var Q125;
            Q125=makeQuery(id+"F4.imprint","IMPRINT",FACE,{"disambiguationData":[TD([[makeQuery(id+"F4.imprint","IMPRINT",EDGE,{"derivedFrom":sQuery(id+"F4.wireOp",EDGE,"E21.sketch_text.stroke-512")}),-1.0]])]});
            var Q126;
            Q126=makeQuery(id+"F4.imprint","IMPRINT",FACE,{"disambiguationData":[TD([[makeQuery(id+"F4.imprint","IMPRINT",EDGE,{"derivedFrom":sQuery(id+"F4.wireOp",EDGE,"E20.sketch_text.stroke-1137")}),-1.0]])]});
            var Q127;
            Q127=makeQuery(id+"F4.imprint","IMPRINT",FACE,{"disambiguationData":[TD([[makeQuery(id+"F4.imprint","IMPRINT",EDGE,{"derivedFrom":sQuery(id+"F4.wireOp",EDGE,"E20.sketch_text.stroke-462")}),-1.0]])]});
            var Q128;
            Q128=makeQuery(id+"F4.imprint","IMPRINT",FACE,{"disambiguationData":[TD([[makeQuery(id+"F4.imprint","IMPRINT",EDGE,{"derivedFrom":sQuery(id+"F4.wireOp",EDGE,"E21.sketch_text.stroke-145")}),-1.0]])]});
            var Q129;
            Q129=makeQuery(id+"F4.imprint","IMPRINT",FACE,{"disambiguationData":[TD([[makeQuery(id+"F4.imprint","IMPRINT",EDGE,{"derivedFrom":sQuery(id+"F4.wireOp",EDGE,"E21.sketch_text.stroke-970")}),1.0]])]});
            var Q130;
            Q130=makeQuery(id+"F4.imprint","IMPRINT",FACE,{"disambiguationData":[TD([[makeQuery(id+"F4.imprint","IMPRINT",EDGE,{"derivedFrom":sQuery(id+"F4.wireOp",EDGE,"E21.sketch_text.stroke-2251")}),-1.0]])]});
            var Q131;
            Q131=makeQuery(id+"F4.imprint","IMPRINT",FACE,{"disambiguationData":[TD([[makeQuery(id+"F4.imprint","IMPRINT",EDGE,{"derivedFrom":sQuery(id+"F4.wireOp",EDGE,"E21.sketch_text.stroke-2072")}),-1.0]])]});
            var Q132;
            Q132=makeQuery(id+"F4.imprint","IMPRINT",FACE,{"disambiguationData":[TD([[makeQuery(id+"F4.imprint","IMPRINT",EDGE,{"derivedFrom":sQuery(id+"F4.wireOp",EDGE,"E21.sketch_text.stroke-1366")}),-1.0]])]});
            var Q133;
            Q133=makeQuery(id+"F4.imprint","IMPRINT",FACE,{"disambiguationData":[TD([[makeQuery(id+"F4.imprint","IMPRINT",EDGE,{"derivedFrom":sQuery(id+"F4.wireOp",EDGE,"E21.sketch_text.stroke-554")}),-1.0]])]});
            var Q134;
            Q134=makeQuery(id+"F4.imprint","IMPRINT",FACE,{"disambiguationData":[TD([[makeQuery(id+"F4.imprint","IMPRINT",EDGE,{"derivedFrom":sQuery(id+"F4.wireOp",EDGE,"E20.sketch_text.stroke-204")}),-1.0]])]});
            var Q135;
            Q135=makeQuery(id+"F4.imprint","IMPRINT",FACE,{"disambiguationData":[TD([[makeQuery(id+"F4.imprint","IMPRINT",EDGE,{"derivedFrom":sQuery(id+"F4.wireOp",EDGE,"E20.sketch_text.stroke-0")}),-1.0]])]});
            var Q136;
            Q136=makeQuery(id+"F4.imprint","IMPRINT",FACE,{"disambiguationData":[TD([[makeQuery(id+"F4.imprint","IMPRINT",EDGE,{"derivedFrom":sQuery(id+"F4.wireOp",EDGE,"E20.sketch_text.stroke-6")}),-1.0]])]});
            var Q137;
            Q137=makeQuery(id+"F4.imprint","IMPRINT",FACE,{"disambiguationData":[TD([[makeQuery(id+"F4.imprint","IMPRINT",EDGE,{"derivedFrom":sQuery(id+"F4.wireOp",EDGE,"E20.sketch_text.stroke-12")}),-1.0]])]});
            var Q138;
            Q138=makeQuery(id+"F4.imprint","IMPRINT",FACE,{"disambiguationData":[TD([[makeQuery(id+"F4.imprint","IMPRINT",EDGE,{"derivedFrom":sQuery(id+"F4.wireOp",EDGE,"E20.sketch_text.stroke-59")}),-1.0]])]});
            var Q139;
            Q139=makeQuery(id+"F4.imprint","IMPRINT",FACE,{"disambiguationData":[TD([[makeQuery(id+"F4.imprint","IMPRINT",EDGE,{"derivedFrom":sQuery(id+"F4.wireOp",EDGE,"E20.sketch_text.stroke-84")}),-1.0]])]});
            var Q140;
            Q140=makeQuery(id+"F4.imprint","IMPRINT",FACE,{"disambiguationData":[TD([[makeQuery(id+"F4.imprint","IMPRINT",EDGE,{"derivedFrom":sQuery(id+"F4.wireOp",EDGE,"E20.sketch_text.stroke-109")}),-1.0]])]});
            var Q141;
            Q141=makeQuery(id+"F4.imprint","IMPRINT",FACE,{"disambiguationData":[TD([[makeQuery(id+"F4.imprint","IMPRINT",EDGE,{"derivedFrom":sQuery(id+"F4.wireOp",EDGE,"E20.sketch_text.stroke-143")}),-1.0]])]});
            var Q142;
            Q142=makeQuery(id+"F4.imprint","IMPRINT",FACE,{"disambiguationData":[TD([[makeQuery(id+"F4.imprint","IMPRINT",EDGE,{"derivedFrom":sQuery(id+"F4.wireOp",EDGE,"E20.sketch_text.stroke-162")}),-1.0]])]});
            var Q143;
            Q143=makeQuery(id+"F4.imprint","IMPRINT",FACE,{"disambiguationData":[TD([[makeQuery(id+"F4.imprint","IMPRINT",EDGE,{"derivedFrom":sQuery(id+"F4.wireOp",EDGE,"E21.sketch_text.stroke-1248")}),-1.0]])]});
            var Q144;
            Q144=makeQuery(id+"F4.imprint","IMPRINT",FACE,{"disambiguationData":[TD([[makeQuery(id+"F4.imprint","IMPRINT",EDGE,{"derivedFrom":sQuery(id+"F4.wireOp",EDGE,"E21.sketch_text.stroke-764")}),-1.0]])]});
            var Q145;
            Q145=makeQuery(id+"F4.imprint","IMPRINT",FACE,{"disambiguationData":[TD([[makeQuery(id+"F4.imprint","IMPRINT",EDGE,{"derivedFrom":sQuery(id+"F4.wireOp",EDGE,"E20.sketch_text.stroke-1303")}),-1.0]])]});
            var Q146;
            Q146=makeQuery(id+"F4.imprint","IMPRINT",FACE,{"disambiguationData":[TD([[makeQuery(id+"F4.imprint","IMPRINT",EDGE,{"derivedFrom":sQuery(id+"F4.wireOp",EDGE,"E20.sketch_text.stroke-658")}),-1.0]])]});
            var Q147;
            Q147=makeQuery(id+"F4.imprint","IMPRINT",FACE,{"disambiguationData":[TD([[makeQuery(id+"F4.imprint","IMPRINT",EDGE,{"derivedFrom":sQuery(id+"F4.wireOp",EDGE,"E21.sketch_text.stroke-2274")}),-1.0]])]});
            var Q148;
            Q148=makeQuery(id+"F4.imprint","IMPRINT",FACE,{"disambiguationData":[TD([[makeQuery(id+"F4.imprint","IMPRINT",EDGE,{"derivedFrom":sQuery(id+"F4.wireOp",EDGE,"E21.sketch_text.stroke-2171")}),-1.0]])]});
            var Q149;
            Q149=makeQuery(id+"F4.imprint","IMPRINT",FACE,{"disambiguationData":[TD([[makeQuery(id+"F4.imprint","IMPRINT",EDGE,{"derivedFrom":sQuery(id+"F4.wireOp",EDGE,"E21.sketch_text.stroke-1524")}),-1.0]])]});
            var Q150;
            Q150=makeQuery(id+"F4.imprint","IMPRINT",FACE,{"disambiguationData":[TD([[makeQuery(id+"F4.imprint","IMPRINT",EDGE,{"derivedFrom":sQuery(id+"F4.wireOp",EDGE,"E20.sketch_text.stroke-1349")}),-1.0]])]});
            var Q151;
            Q151=makeQuery(id+"F4.imprint","IMPRINT",FACE,{"disambiguationData":[TD([[makeQuery(id+"F4.imprint","IMPRINT",EDGE,{"derivedFrom":sQuery(id+"F4.wireOp",EDGE,"E20.sketch_text.stroke-1119")}),-1.0]])]});
            var Q152;
            Q152=makeQuery(id+"F4.imprint","IMPRINT",FACE,{"disambiguationData":[TD([[makeQuery(id+"F4.imprint","IMPRINT",EDGE,{"derivedFrom":sQuery(id+"F4.wireOp",EDGE,"E20.sketch_text.stroke-796")}),-1.0]])]});
            var Q153;
            Q153=makeQuery(id+"F4.imprint","IMPRINT",FACE,{"disambiguationData":[TD([[makeQuery(id+"F4.imprint","IMPRINT",EDGE,{"derivedFrom":sQuery(id+"F4.wireOp",EDGE,"E20.sketch_text.stroke-493")}),-1.0]])]});
            var Q154;
            Q154=makeQuery(id+"F4.imprint","IMPRINT",FACE,{"disambiguationData":[TD([[makeQuery(id+"F4.imprint","IMPRINT",EDGE,{"derivedFrom":sQuery(id+"F4.wireOp",EDGE,"E21.sketch_text.stroke-1007")}),-1.0]])]});
            var Q155;
            Q155=makeQuery(id+"F4.imprint","IMPRINT",FACE,{"disambiguationData":[TD([[makeQuery(id+"F4.imprint","IMPRINT",EDGE,{"derivedFrom":sQuery(id+"F4.wireOp",EDGE,"E20.sketch_text.stroke-1083")}),-1.0]])]});
            var Q156;
            Q156=makeQuery(id+"F4.imprint","IMPRINT",FACE,{"disambiguationData":[TD([[makeQuery(id+"F4.imprint","IMPRINT",EDGE,{"derivedFrom":sQuery(id+"F4.wireOp",EDGE,"E20.sketch_text.stroke-760")}),-1.0]])]});
            var Q157;
            Q157=makeQuery(id+"F4.imprint","IMPRINT",FACE,{"disambiguationData":[TD([[makeQuery(id+"F4.imprint","IMPRINT",EDGE,{"derivedFrom":sQuery(id+"F4.wireOp",EDGE,"E20.sketch_text.stroke-481")}),-1.0]])]});
            var Q158;
            Q158=makeQuery(id+"F4.imprint","IMPRINT",FACE,{"disambiguationData":[TD([[makeQuery(id+"F4.imprint","IMPRINT",EDGE,{"derivedFrom":sQuery(id+"F4.wireOp",EDGE,"E21.sketch_text.stroke-702")}),1.0]])]});
            var Q159;
            Q159=makeQuery(id+"F4.imprint","IMPRINT",FACE,{"disambiguationData":[TD([[makeQuery(id+"F4.imprint","IMPRINT",EDGE,{"derivedFrom":sQuery(id+"F4.wireOp",EDGE,"E21.sketch_text.stroke-410")}),-1.0]])]});
            var Q160;
            Q160=makeQuery(id+"F4.imprint","IMPRINT",FACE,{"disambiguationData":[TD([[makeQuery(id+"F4.imprint","IMPRINT",EDGE,{"derivedFrom":sQuery(id+"F4.wireOp",EDGE,"E21.sketch_text.stroke-1715")}),-1.0]])]});
            var Q161;
            Q161=makeQuery(id+"F4.imprint","IMPRINT",FACE,{"disambiguationData":[TD([[makeQuery(id+"F4.imprint","IMPRINT",EDGE,{"derivedFrom":sQuery(id+"F4.wireOp",EDGE,"E21.sketch_text.stroke-1448")}),-1.0]])]});
            var Q162;
            Q162=makeQuery(id+"F4.imprint","IMPRINT",FACE,{"disambiguationData":[TD([[makeQuery(id+"F4.imprint","IMPRINT",EDGE,{"derivedFrom":sQuery(id+"F4.wireOp",EDGE,"E21.sketch_text.stroke-975")}),-1.0]])]});
            var Q163;
            Q163=makeQuery(id+"F4.imprint","IMPRINT",FACE,{"disambiguationData":[TD([[makeQuery(id+"F4.imprint","IMPRINT",EDGE,{"derivedFrom":sQuery(id+"F4.wireOp",EDGE,"E20.sketch_text.stroke-1210")}),-1.0]])]});
            var Q164;
            Q164=makeQuery(id+"F4.imprint","IMPRINT",FACE,{"disambiguationData":[TD([[makeQuery(id+"F4.imprint","IMPRINT",EDGE,{"derivedFrom":sQuery(id+"F4.wireOp",EDGE,"E20.sketch_text.stroke-572")}),-1.0]])]});
            var Q165;
            Q165=makeQuery(id+"F4.imprint","IMPRINT",FACE,{"disambiguationData":[TD([[makeQuery(id+"F4.imprint","IMPRINT",EDGE,{"derivedFrom":sQuery(id+"F4.wireOp",EDGE,"E21.sketch_text.stroke-2261")}),-1.0]])]});
            var Q166;
            Q166=makeQuery(id+"F4.imprint","IMPRINT",FACE,{"disambiguationData":[TD([[makeQuery(id+"F4.imprint","IMPRINT",EDGE,{"derivedFrom":sQuery(id+"F4.wireOp",EDGE,"E21.sketch_text.stroke-1993")}),-1.0]])]});
            var Q167;
            Q167=makeQuery(id+"F4.imprint","IMPRINT",FACE,{"disambiguationData":[TD([[makeQuery(id+"F4.imprint","IMPRINT",EDGE,{"derivedFrom":sQuery(id+"F4.wireOp",EDGE,"E21.sketch_text.stroke-2114")}),-1.0]])]});
            var Q168;
            Q168=makeQuery(id+"F4.imprint","IMPRINT",FACE,{"disambiguationData":[TD([[makeQuery(id+"F4.imprint","IMPRINT",EDGE,{"derivedFrom":sQuery(id+"F4.wireOp",EDGE,"E21.sketch_text.stroke-1429")}),-1.0]])]});
            var Q169;
            Q169=makeQuery(id+"F4.imprint","IMPRINT",FACE,{"disambiguationData":[TD([[makeQuery(id+"F4.imprint","IMPRINT",EDGE,{"derivedFrom":sQuery(id+"F4.wireOp",EDGE,"E21.sketch_text.stroke-664")}),-1.0]])]});
            var Q170;
            Q170=makeQuery(id+"F4.imprint","IMPRINT",FACE,{"disambiguationData":[TD([[makeQuery(id+"F4.imprint","IMPRINT",EDGE,{"derivedFrom":sQuery(id+"F4.wireOp",EDGE,"E20.sketch_text.stroke-1100")}),-1.0]])]});
            var Q171;
            Q171=makeQuery(id+"F4.imprint","IMPRINT",FACE,{"disambiguationData":[TD([[makeQuery(id+"F4.imprint","IMPRINT",EDGE,{"derivedFrom":sQuery(id+"F4.wireOp",EDGE,"E20.sketch_text.stroke-485")}),-1.0]])]});
            var Q172;
            Q172=makeQuery(id+"F4.imprint","IMPRINT",FACE,{"disambiguationData":[TD([[makeQuery(id+"F4.imprint","IMPRINT",EDGE,{"derivedFrom":sQuery(id+"F4.wireOp",EDGE,"E21.sketch_text.stroke-707")}),-1.0]])]});
            var Q173;
            Q173=makeQuery(id+"F4.imprint","IMPRINT",FACE,{"disambiguationData":[TD([[makeQuery(id+"F4.imprint","IMPRINT",EDGE,{"derivedFrom":sQuery(id+"F4.wireOp",EDGE,"E21.sketch_text.stroke-427")}),-1.0]])]});
            var Q174;
            Q174=makeQuery(id+"F4.imprint","IMPRINT",FACE,{"disambiguationData":[TD([[makeQuery(id+"F4.imprint","IMPRINT",EDGE,{"derivedFrom":sQuery(id+"F4.wireOp",EDGE,"E20.sketch_text.stroke-1345")}),-1.0]])]});
            var Q175;
            Q175=makeQuery(id+"F4.imprint","IMPRINT",FACE,{"disambiguationData":[TD([[makeQuery(id+"F4.imprint","IMPRINT",EDGE,{"derivedFrom":sQuery(id+"F4.wireOp",EDGE,"E21.sketch_text.stroke-1722")}),-1.0]])]});
            var Q176;
            Q176=makeQuery(id+"F4.imprint","IMPRINT",FACE,{"disambiguationData":[TD([[makeQuery(id+"F4.imprint","IMPRINT",EDGE,{"derivedFrom":sQuery(id+"F4.wireOp",EDGE,"E21.sketch_text.stroke-1235")}),-1.0]])]});
            var Q177;
            Q177=makeQuery(id+"F4.imprint","IMPRINT",FACE,{"disambiguationData":[TD([[makeQuery(id+"F4.imprint","IMPRINT",EDGE,{"derivedFrom":sQuery(id+"F4.wireOp",EDGE,"E21.sketch_text.stroke-1002")}),1.0]])]});
            var Q178;
            Q178=makeQuery(id+"F4.imprint","IMPRINT",FACE,{"disambiguationData":[TD([[makeQuery(id+"F4.imprint","IMPRINT",EDGE,{"derivedFrom":sQuery(id+"F4.wireOp",EDGE,"E20.sketch_text.stroke-1279")}),-1.0]])]});
            var Q179;
            Q179=makeQuery(id+"F4.imprint","IMPRINT",FACE,{"disambiguationData":[TD([[makeQuery(id+"F4.imprint","IMPRINT",EDGE,{"derivedFrom":sQuery(id+"F4.wireOp",EDGE,"E20.sketch_text.stroke-597")}),-1.0]])]});
            var Q180;
            Q180=makeQuery(id+"F4.imprint","IMPRINT",FACE,{"disambiguationData":[TD([[makeQuery(id+"F4.imprint","IMPRINT",EDGE,{"derivedFrom":sQuery(id+"F4.wireOp",EDGE,"E21.sketch_text.stroke-2270")}),-1.0]])]});
            var Q181;
            Q181=makeQuery(id+"F4.imprint","IMPRINT",FACE,{"disambiguationData":[TD([[makeQuery(id+"F4.imprint","IMPRINT",EDGE,{"derivedFrom":sQuery(id+"F4.wireOp",EDGE,"E21.sketch_text.stroke-2139")}),-1.0]])]});
            var Q182;
            Q182=makeQuery(id+"F4.imprint","IMPRINT",FACE,{"disambiguationData":[TD([[makeQuery(id+"F4.imprint","IMPRINT",EDGE,{"derivedFrom":sQuery(id+"F4.wireOp",EDGE,"E21.sketch_text.stroke-1477")}),-1.0]])]});
            var Q183;
            Q183=makeQuery(id+"F4.imprint","IMPRINT",FACE,{"disambiguationData":[TD([[makeQuery(id+"F4.imprint","IMPRINT",EDGE,{"derivedFrom":sQuery(id+"F4.wireOp",EDGE,"E21.sketch_text.stroke-688")}),-1.0]])]});
            var Q184;
            Q184=makeQuery(id+"F4.imprint","IMPRINT",FACE,{"disambiguationData":[TD([[makeQuery(id+"F4.imprint","IMPRINT",EDGE,{"derivedFrom":sQuery(id+"F4.wireOp",EDGE,"E20.sketch_text.stroke-1151")}),1.0]])]});
            var Q185;
            Q185=makeQuery(id+"F4.imprint","IMPRINT",FACE,{"disambiguationData":[TD([[makeQuery(id+"F4.imprint","IMPRINT",EDGE,{"derivedFrom":sQuery(id+"F4.wireOp",EDGE,"E20.sketch_text.stroke-815")}),-1.0]])]});
            var Q186;
            Q186=makeQuery(id+"F4.imprint","IMPRINT",FACE,{"disambiguationData":[TD([[makeQuery(id+"F4.imprint","IMPRINT",EDGE,{"derivedFrom":sQuery(id+"F4.wireOp",EDGE,"E20.sketch_text.stroke-277")}),1.0]])]});
            var Q187;
            Q187=makeQuery(id+"F4.imprint","IMPRINT",FACE,{"disambiguationData":[TD([[makeQuery(id+"F4.imprint","IMPRINT",EDGE,{"derivedFrom":sQuery(id+"F4.wireOp",EDGE,"E21.sketch_text.stroke-751")}),-1.0]])]});
            var Q188;
            Q188=makeQuery(id+"F4.imprint","IMPRINT",FACE,{"disambiguationData":[TD([[makeQuery(id+"F4.imprint","IMPRINT",EDGE,{"derivedFrom":sQuery(id+"F4.wireOp",EDGE,"E21.sketch_text.stroke-223")}),-1.0]])]});
            var Q189;
            Q189=makeQuery(id+"F4.imprint","IMPRINT",FACE,{"disambiguationData":[TD([[makeQuery(id+"F4.imprint","IMPRINT",EDGE,{"derivedFrom":sQuery(id+"F4.wireOp",EDGE,"E20.sketch_text.stroke-1353")}),-1.0]])]});
            var Q190;
            Q190=makeQuery(id+"F4.imprint","IMPRINT",FACE,{"disambiguationData":[TD([[makeQuery(id+"F4.imprint","IMPRINT",EDGE,{"derivedFrom":sQuery(id+"F4.wireOp",EDGE,"E21.sketch_text.stroke-1774")}),-1.0]])]});
            var Q191;
            Q191=makeQuery(id+"F4.imprint","IMPRINT",FACE,{"disambiguationData":[TD([[makeQuery(id+"F4.imprint","IMPRINT",EDGE,{"derivedFrom":sQuery(id+"F4.wireOp",EDGE,"E21.sketch_text.stroke-1496")}),-1.0]])]});
            var Q192;
            Q192=makeQuery(id+"F4.imprint","IMPRINT",FACE,{"disambiguationData":[TD([[makeQuery(id+"F4.imprint","IMPRINT",EDGE,{"derivedFrom":sQuery(id+"F4.wireOp",EDGE,"E21.sketch_text.stroke-27")}),-1.0]])]});
            var Q193;
            Q193=makeQuery(id+"F4.imprint","IMPRINT",FACE,{"disambiguationData":[TD([[makeQuery(id+"F4.imprint","IMPRINT",EDGE,{"derivedFrom":sQuery(id+"F4.wireOp",EDGE,"E20.sketch_text.stroke-683")}),-1.0]])]});
            var Q194;
            Q194=makeQuery(id+"F4.imprint","IMPRINT",FACE,{"disambiguationData":[TD([[makeQuery(id+"F4.imprint","IMPRINT",EDGE,{"derivedFrom":sQuery(id+"F4.wireOp",EDGE,"E20.sketch_text.stroke-32")}),-1.0]])]});
            var Q195;
            Q195=makeQuery(id+"F4.imprint","IMPRINT",FACE,{"disambiguationData":[TD([[makeQuery(id+"F4.imprint","IMPRINT",EDGE,{"derivedFrom":sQuery(id+"F4.wireOp",EDGE,"E21.sketch_text.stroke-2059")}),-1.0]])]});
            var Q196;
            Q196=makeQuery(id+"F4.imprint","IMPRINT",FACE,{"disambiguationData":[TD([[makeQuery(id+"F4.imprint","IMPRINT",EDGE,{"derivedFrom":sQuery(id+"F4.wireOp",EDGE,"E20.sketch_text.stroke-1003")}),-1.0]])]});
            var Q197;
            Q197=makeQuery(id+"F4.imprint","IMPRINT",FACE,{"disambiguationData":[TD([[makeQuery(id+"F4.imprint","IMPRINT",EDGE,{"derivedFrom":sQuery(id+"F4.wireOp",EDGE,"E21.sketch_text.stroke-1580")}),-1.0]])]});
            var Q198;
            Q198=makeQuery(id+"F4.imprint","IMPRINT",FACE,{"disambiguationData":[TD([[makeQuery(id+"F4.imprint","IMPRINT",EDGE,{"derivedFrom":sQuery(id+"F4.wireOp",EDGE,"E21.sketch_text.stroke-797")}),-1.0]])]});
            var Q199;
            Q199=makeQuery(id+"F4.imprint","IMPRINT",FACE,{"disambiguationData":[TD([[makeQuery(id+"F4.imprint","IMPRINT",EDGE,{"derivedFrom":sQuery(id+"F4.wireOp",EDGE,"E20.sketch_text.stroke-535")}),-1.0]])]});
            var Q200;
            Q200=makeQuery(id+"F4.imprint","IMPRINT",FACE,{"disambiguationData":[TD([[makeQuery(id+"F4.imprint","IMPRINT",EDGE,{"derivedFrom":sQuery(id+"F4.wireOp",EDGE,"E21.sketch_text.stroke-255")}),1.0]])]});
            var Q201;
            Q201=makeQuery(id+"F4.imprint","IMPRINT",FACE,{"disambiguationData":[TD([[makeQuery(id+"F4.imprint","IMPRINT",EDGE,{"derivedFrom":sQuery(id+"F4.wireOp",EDGE,"E20.sketch_text.stroke-1357")}),-1.0]])]});
            var Q202;
            Q202=makeQuery(id+"F4.imprint","IMPRINT",FACE,{"disambiguationData":[TD([[makeQuery(id+"F4.imprint","IMPRINT",EDGE,{"derivedFrom":sQuery(id+"F4.wireOp",EDGE,"E21.sketch_text.stroke-1805")}),1.0]])]});
            var Q203;
            Q203=makeQuery(id+"F4.imprint","IMPRINT",FACE,{"disambiguationData":[TD([[makeQuery(id+"F4.imprint","IMPRINT",EDGE,{"derivedFrom":sQuery(id+"F4.wireOp",EDGE,"E21.sketch_text.stroke-1260")}),-1.0]])]});
            var Q204;
            Q204=makeQuery(id+"F4.imprint","IMPRINT",FACE,{"disambiguationData":[TD([[makeQuery(id+"F4.imprint","IMPRINT",EDGE,{"derivedFrom":sQuery(id+"F4.wireOp",EDGE,"E21.sketch_text.stroke-164")}),-1.0]])]});
            var Q205;
            Q205=makeQuery(id+"F4.imprint","IMPRINT",FACE,{"disambiguationData":[TD([[makeQuery(id+"F4.imprint","IMPRINT",EDGE,{"derivedFrom":sQuery(id+"F4.wireOp",EDGE,"E20.sketch_text.stroke-717")}),-1.0]])]});
            var Q206;
            Q206=makeQuery(id+"F4.imprint","IMPRINT",FACE,{"disambiguationData":[TD([[makeQuery(id+"F4.imprint","IMPRINT",EDGE,{"derivedFrom":sQuery(id+"F4.wireOp",EDGE,"E20.sketch_text.stroke-126")}),-1.0]])]});
            var Q207;
            Q207=makeQuery(id+"F4.imprint","IMPRINT",FACE,{"disambiguationData":[TD([[makeQuery(id+"F4.imprint","IMPRINT",EDGE,{"derivedFrom":sQuery(id+"F4.wireOp",EDGE,"E21.sketch_text.stroke-101")}),-1.0]])]});
            var Q208;
            Q208=makeQuery(id+"F4.imprint","IMPRINT",FACE,{"disambiguationData":[TD([[makeQuery(id+"F4.imprint","IMPRINT",EDGE,{"derivedFrom":sQuery(id+"F4.wireOp",EDGE,"E21.sketch_text.stroke-1605")}),-1.0]])]});
            var Q209;
            Q209=makeQuery(id+"F4.imprint","IMPRINT",FACE,{"disambiguationData":[TD([[makeQuery(id+"F4.imprint","IMPRINT",EDGE,{"derivedFrom":sQuery(id+"F4.wireOp",EDGE,"E21.sketch_text.stroke-816")}),-1.0]])]});
            var Q210;
            Q210=makeQuery(id+"F4.imprint","IMPRINT",FACE,{"disambiguationData":[TD([[makeQuery(id+"F4.imprint","IMPRINT",EDGE,{"derivedFrom":sQuery(id+"F4.wireOp",EDGE,"E20.sketch_text.stroke-1173")}),-1.0]])]});
            var Q211;
            Q211=makeQuery(id+"F4.imprint","IMPRINT",FACE,{"disambiguationData":[TD([[makeQuery(id+"F4.imprint","IMPRINT",EDGE,{"derivedFrom":sQuery(id+"F4.wireOp",EDGE,"E20.sketch_text.stroke-552")}),-1.0]])]});
            var Q212;
            Q212=makeQuery(id+"F4.imprint","IMPRINT",FACE,{"disambiguationData":[TD([[makeQuery(id+"F4.imprint","IMPRINT",EDGE,{"derivedFrom":sQuery(id+"F4.wireOp",EDGE,"E20.sketch_text.stroke-309")}),-1.0]])]});
            var Q213;
            Q213=makeQuery(id+"F4.imprint","IMPRINT",FACE,{"disambiguationData":[TD([[makeQuery(id+"F4.imprint","IMPRINT",EDGE,{"derivedFrom":sQuery(id+"F4.wireOp",EDGE,"E21.sketch_text.stroke-781")}),-1.0]])]});
            var Q214;
            Q214=makeQuery(id+"F4.imprint","IMPRINT",FACE,{"disambiguationData":[TD([[makeQuery(id+"F4.imprint","IMPRINT",EDGE,{"derivedFrom":sQuery(id+"F4.wireOp",EDGE,"E21.sketch_text.stroke-495")}),-1.0]])]});
            var Q215;
            Q215=makeQuery(id+"F4.imprint","IMPRINT",FACE,{"disambiguationData":[TD([[makeQuery(id+"F4.imprint","IMPRINT",EDGE,{"derivedFrom":sQuery(id+"F4.wireOp",EDGE,"E21.sketch_text.stroke-260")}),-1.0]])]});
            var Q216;
            Q216=makeQuery(id+"F4.imprint","IMPRINT",FACE,{"disambiguationData":[TD([[makeQuery(id+"F4.imprint","IMPRINT",EDGE,{"derivedFrom":sQuery(id+"F4.wireOp",EDGE,"E21.sketch_text.stroke-0")}),-1.0]])]});
            var Q217;
            Q217=makeQuery(id+"F4.imprint","IMPRINT",FACE,{"disambiguationData":[TD([[makeQuery(id+"F4.imprint","IMPRINT",EDGE,{"derivedFrom":sQuery(id+"F4.wireOp",EDGE,"E21.sketch_text.stroke-1810")}),-1.0]])]});
            var Q218;
            Q218=makeQuery(id+"F4.imprint","IMPRINT",FACE,{"disambiguationData":[TD([[makeQuery(id+"F4.imprint","IMPRINT",EDGE,{"derivedFrom":sQuery(id+"F4.wireOp",EDGE,"E21.sketch_text.stroke-1551")}),-1.0]])]});
            var Q219;
            Q219=makeQuery(id+"F4.imprint","IMPRINT",FACE,{"disambiguationData":[TD([[makeQuery(id+"F4.imprint","IMPRINT",EDGE,{"derivedFrom":sQuery(id+"F4.wireOp",EDGE,"E21.sketch_text.stroke-181")}),-1.0]])]});
            var Q220;
            Q220=makeQuery(id+"F4.imprint","IMPRINT",FACE,{"disambiguationData":[TD([[makeQuery(id+"F4.imprint","IMPRINT",EDGE,{"derivedFrom":sQuery(id+"F4.wireOp",EDGE,"E20.sketch_text.stroke-736")}),-1.0]])]});
            var Q221;
            Q221=makeQuery(id+"F4.imprint","IMPRINT",FACE,{"disambiguationData":[TD([[makeQuery(id+"F4.imprint","IMPRINT",EDGE,{"derivedFrom":sQuery(id+"F4.wireOp",EDGE,"E20.sketch_text.stroke-187")}),-1.0]])]});
            var Q222;
            Q222=makeQuery(id+"F4.imprint","IMPRINT",FACE,{"disambiguationData":[TD([[makeQuery(id+"F4.imprint","IMPRINT",EDGE,{"derivedFrom":sQuery(id+"F4.wireOp",EDGE,"E21.sketch_text.stroke-2089")}),-1.0]])]});
            var Q223;
            Q223=makeQuery(id+"F4.imprint","IMPRINT",FACE,{"disambiguationData":[TD([[makeQuery(id+"F4.imprint","IMPRINT",EDGE,{"derivedFrom":sQuery(id+"F4.wireOp",EDGE,"E21.sketch_text.stroke-620")}),-1.0]])]});
            var Q224;
            Q224=makeQuery(id+"F4.imprint","IMPRINT",FACE,{"disambiguationData":[TD([[makeQuery(id+"F4.imprint","IMPRINT",EDGE,{"derivedFrom":sQuery(id+"F4.wireOp",EDGE,"E21.sketch_text.stroke-1645")}),-1.0]])]});
            var Q225;
            Q225=makeQuery(id+"F4.imprint","IMPRINT",FACE,{"disambiguationData":[TD([[makeQuery(id+"F4.imprint","IMPRINT",EDGE,{"derivedFrom":sQuery(id+"F4.wireOp",EDGE,"E21.sketch_text.stroke-840")}),-1.0]])]});
            var Q226;
            Q226=makeQuery(id+"F4.imprint","IMPRINT",FACE,{"disambiguationData":[TD([[makeQuery(id+"F4.imprint","IMPRINT",EDGE,{"derivedFrom":sQuery(id+"F4.wireOp",EDGE,"E20.sketch_text.stroke-556")}),-1.0]])]});
            var Q227;
            Q227=makeQuery(id+"F4.imprint","IMPRINT",FACE,{"disambiguationData":[TD([[makeQuery(id+"F4.imprint","IMPRINT",EDGE,{"derivedFrom":sQuery(id+"F4.wireOp",EDGE,"E21.sketch_text.stroke-1817")}),-1.0]])]});
            var Q228;
            Q228=makeQuery(id+"F4.imprint","IMPRINT",FACE,{"disambiguationData":[TD([[makeQuery(id+"F4.imprint","IMPRINT",EDGE,{"derivedFrom":sQuery(id+"F4.wireOp",EDGE,"E21.sketch_text.stroke-1294")}),-1.0]])]});
            var Q229;
            Q229=makeQuery(id+"F4.imprint","IMPRINT",FACE,{"disambiguationData":[TD([[makeQuery(id+"F4.imprint","IMPRINT",EDGE,{"derivedFrom":sQuery(id+"F4.wireOp",EDGE,"E21.sketch_text.stroke-204")}),-1.0]])]});
            var Q230;
            Q230=makeQuery(id+"F4.imprint","IMPRINT",FACE,{"disambiguationData":[TD([[makeQuery(id+"F4.imprint","IMPRINT",EDGE,{"derivedFrom":sQuery(id+"F4.wireOp",EDGE,"E20.sketch_text.stroke-779")}),-1.0]])]});
            var Q231;
            Q231=makeQuery(id+"F4.imprint","IMPRINT",FACE,{"disambiguationData":[TD([[makeQuery(id+"F4.imprint","IMPRINT",EDGE,{"derivedFrom":sQuery(id+"F4.wireOp",EDGE,"E20.sketch_text.stroke-223")}),-1.0]])]});
            var Q232;
            Q232=makeQuery(id+"F4.imprint","IMPRINT",FACE,{"disambiguationData":[TD([[makeQuery(id+"F4.imprint","IMPRINT",EDGE,{"derivedFrom":sQuery(id+"F4.wireOp",EDGE,"E21.sketch_text.stroke-1747")}),-1.0]])]});
            var Q233;
            Q233=makeQuery(id+"F4.imprint","IMPRINT",FACE,{"disambiguationData":[TD([[makeQuery(id+"F4.imprint","IMPRINT",EDGE,{"derivedFrom":sQuery(id+"F4.wireOp",EDGE,"E21.sketch_text.stroke-916")}),-1.0]])]});
            var Q234;
            Q234=makeQuery(id+"F4.imprint","IMPRINT",FACE,{"disambiguationData":[TD([[makeQuery(id+"F4.imprint","IMPRINT",EDGE,{"derivedFrom":sQuery(id+"F4.wireOp",EDGE,"E20.sketch_text.stroke-903")}),-1.0]])]});
            var Q235;
            Q235=makeQuery(id+"F4.imprint","IMPRINT",FACE,{"disambiguationData":[TD([[makeQuery(id+"F4.imprint","IMPRINT",EDGE,{"derivedFrom":sQuery(id+"F4.wireOp",EDGE,"E20.sketch_text.stroke-336")}),-1.0]])]});
            var Q236;
            Q236=makeQuery(id+"F4.imprint","IMPRINT",FACE,{"disambiguationData":[TD([[makeQuery(id+"F4.imprint","IMPRINT",EDGE,{"derivedFrom":sQuery(id+"F4.wireOp",EDGE,"E21.sketch_text.stroke-536")}),-1.0]])]});
            var Q237;
            Q237=makeQuery(id+"F4.imprint","IMPRINT",FACE,{"disambiguationData":[TD([[makeQuery(id+"F4.imprint","IMPRINT",EDGE,{"derivedFrom":sQuery(id+"F4.wireOp",EDGE,"E21.sketch_text.stroke-288")}),-1.0]])]});
            var Q238;
            Q238=makeQuery(id+"F4.imprint","IMPRINT",FACE,{"disambiguationData":[TD([[makeQuery(id+"F4.imprint","IMPRINT",EDGE,{"derivedFrom":sQuery(id+"F4.wireOp",EDGE,"E21.sketch_text.stroke-12")}),-1.0]])]});
            var Q239;
            Q239=makeQuery(id+"F4.imprint","IMPRINT",FACE,{"disambiguationData":[TD([[makeQuery(id+"F4.imprint","IMPRINT",EDGE,{"derivedFrom":sQuery(id+"F4.wireOp",EDGE,"E21.sketch_text.stroke-1563")}),-1.0]])]});
            var Q240;
            Q240=makeQuery(id+"F4.imprint","IMPRINT",FACE,{"disambiguationData":[TD([[makeQuery(id+"F4.imprint","IMPRINT",EDGE,{"derivedFrom":sQuery(id+"F4.wireOp",EDGE,"E21.sketch_text.stroke-1298")}),-1.0]])]});
            var Q241;
            Q241=makeQuery(id+"F4.imprint","IMPRINT",FACE,{"disambiguationData":[TD([[makeQuery(id+"F4.imprint","IMPRINT",EDGE,{"derivedFrom":sQuery(id+"F4.wireOp",EDGE,"E21.sketch_text.stroke-241")}),-1.0]])]});
            var Q242;
            Q242=makeQuery(id+"F4.imprint","IMPRINT",FACE,{"disambiguationData":[TD([[makeQuery(id+"F4.imprint","IMPRINT",EDGE,{"derivedFrom":sQuery(id+"F4.wireOp",EDGE,"E20.sketch_text.stroke-833")}),-1.0]])]});
            var Q243;
            Q243=makeQuery(id+"F4.imprint","IMPRINT",FACE,{"disambiguationData":[TD([[makeQuery(id+"F4.imprint","IMPRINT",EDGE,{"derivedFrom":sQuery(id+"F4.wireOp",EDGE,"E20.sketch_text.stroke-240")}),-1.0]])]});
            var Q244;
            Q244=makeQuery(id+"F4.imprint","IMPRINT",FACE,{"disambiguationData":[TD([[makeQuery(id+"F4.imprint","IMPRINT",EDGE,{"derivedFrom":sQuery(id+"F4.wireOp",EDGE,"E21.sketch_text.stroke-1791")}),-1.0]])]});
            var Q245;
            Q245=makeQuery(id+"F4.imprint","IMPRINT",FACE,{"disambiguationData":[TD([[makeQuery(id+"F4.imprint","IMPRINT",EDGE,{"derivedFrom":sQuery(id+"F4.wireOp",EDGE,"E21.sketch_text.stroke-956")}),-1.0]])]});
            var Q246;
            Q246=makeQuery(id+"F4.imprint","IMPRINT",FACE,{"disambiguationData":[TD([[makeQuery(id+"F4.imprint","IMPRINT",EDGE,{"derivedFrom":sQuery(id+"F4.wireOp",EDGE,"E20.sketch_text.stroke-1229")}),-1.0]])]});
            var Q247;
            Q247=makeQuery(id+"F4.imprint","IMPRINT",FACE,{"disambiguationData":[TD([[makeQuery(id+"F4.imprint","IMPRINT",EDGE,{"derivedFrom":sQuery(id+"F4.wireOp",EDGE,"E21.sketch_text.stroke-292")}),-1.0]])]});
            var Q248;
            Q248=makeQuery(id+"F4.imprint","IMPRINT",FACE,{"disambiguationData":[TD([[makeQuery(id+"F4.imprint","IMPRINT",EDGE,{"derivedFrom":sQuery(id+"F4.wireOp",EDGE,"E21.sketch_text.stroke-1852")}),-1.0]])]});
            var Q249;
            Q249=makeQuery(id+"F4.imprint","IMPRINT",FACE,{"disambiguationData":[TD([[makeQuery(id+"F4.imprint","IMPRINT",EDGE,{"derivedFrom":sQuery(id+"F4.wireOp",EDGE,"E21.sketch_text.stroke-1091")}),-1.0]])]});
            var Q250;
            Q250=makeQuery(id+"F4.imprint","IMPRINT",FACE,{"disambiguationData":[TD([[makeQuery(id+"F4.imprint","IMPRINT",EDGE,{"derivedFrom":sQuery(id+"F4.wireOp",EDGE,"E21.sketch_text.stroke-264")}),-1.0]])]});
            var Q251;
            Q251=makeQuery(id+"F4.imprint","IMPRINT",FACE,{"disambiguationData":[TD([[makeQuery(id+"F4.imprint","IMPRINT",EDGE,{"derivedFrom":sQuery(id+"F4.wireOp",EDGE,"E20.sketch_text.stroke-852")}),-1.0]])]});
            var Q252;
            Q252=makeQuery(id+"F4.imprint","IMPRINT",FACE,{"disambiguationData":[TD([[makeQuery(id+"F4.imprint","IMPRINT",EDGE,{"derivedFrom":sQuery(id+"F4.wireOp",EDGE,"E20.sketch_text.stroke-263")}),-1.0]])]});
            var Q253;
            Q253=makeQuery(id+"F4.imprint","IMPRINT",FACE,{"disambiguationData":[TD([[makeQuery(id+"F4.imprint","IMPRINT",EDGE,{"derivedFrom":sQuery(id+"F4.wireOp",EDGE,"E21.sketch_text.stroke-2158")}),-1.0]])]});
            var Q254;
            Q254=makeQuery(id+"F4.imprint","IMPRINT",FACE,{"disambiguationData":[TD([[makeQuery(id+"F4.imprint","IMPRINT",EDGE,{"derivedFrom":sQuery(id+"F4.wireOp",EDGE,"E21.sketch_text.stroke-1835")}),-1.0]])]});
            var Q255;
            Q255=makeQuery(id+"F4.imprint","IMPRINT",FACE,{"disambiguationData":[TD([[makeQuery(id+"F4.imprint","IMPRINT",EDGE,{"derivedFrom":sQuery(id+"F4.wireOp",EDGE,"E21.sketch_text.stroke-988")}),-1.0]])]});
            var Q256;
            Q256=makeQuery(id+"F4.imprint","IMPRINT",FACE,{"disambiguationData":[TD([[makeQuery(id+"F4.imprint","IMPRINT",EDGE,{"derivedFrom":sQuery(id+"F4.wireOp",EDGE,"E21.sketch_text.stroke-317")}),-1.0]])]});
            var Q257;
            Q257=makeQuery(id+"F4.imprint","IMPRINT",FACE,{"disambiguationData":[TD([[makeQuery(id+"F4.imprint","IMPRINT",EDGE,{"derivedFrom":sQuery(id+"F4.wireOp",EDGE,"E21.sketch_text.stroke-72")}),-1.0]])]});
            var Q258;
            Q258=makeQuery(id+"F4.imprint","IMPRINT",FACE,{"disambiguationData":[TD([[makeQuery(id+"F4.imprint","IMPRINT",EDGE,{"derivedFrom":sQuery(id+"F4.wireOp",EDGE,"E21.sketch_text.stroke-1380")}),1.0]])]});
            var Q259;
            Q259=makeQuery(id+"F4.imprint","IMPRINT",FACE,{"disambiguationData":[TD([[makeQuery(id+"F4.imprint","IMPRINT",EDGE,{"derivedFrom":sQuery(id+"F4.wireOp",EDGE,"E21.sketch_text.stroke-595")}),-1.0]])]});
            var Q260;
            Q260=makeQuery(id+"F4.imprint","IMPRINT",FACE,{"disambiguationData":[TD([[makeQuery(id+"F4.imprint","IMPRINT",EDGE,{"derivedFrom":sQuery(id+"F4.wireOp",EDGE,"E21.sketch_text.stroke-1903")}),-1.0]])]});
            var Q261;
            Q261=makeQuery(id+"F4.imprint","IMPRINT",FACE,{"disambiguationData":[TD([[makeQuery(id+"F4.imprint","IMPRINT",EDGE,{"derivedFrom":sQuery(id+"F4.wireOp",EDGE,"E21.sketch_text.stroke-1659")}),1.0]])]});
            var Q262;
            Q262=makeQuery(id+"F4.imprint","IMPRINT",FACE,{"disambiguationData":[TD([[makeQuery(id+"F4.imprint","IMPRINT",EDGE,{"derivedFrom":sQuery(id+"F4.wireOp",EDGE,"E21.sketch_text.stroke-344")}),1.0]])]});
            var Q263;
            Q263=makeQuery(id+"F4.imprint","IMPRINT",FACE,{"disambiguationData":[TD([[makeQuery(id+"F4.imprint","IMPRINT",EDGE,{"derivedFrom":sQuery(id+"F4.wireOp",EDGE,"E20.sketch_text.stroke-1271")}),-1.0]])]});
            var Q264;
            Q264=makeQuery(id+"F4.imprint","IMPRINT",FACE,{"disambiguationData":[TD([[makeQuery(id+"F4.imprint","IMPRINT",EDGE,{"derivedFrom":sQuery(id+"F4.wireOp",EDGE,"E21.sketch_text.stroke-2230")}),-1.0]])]});
            var Q265;
            Q265=makeQuery(id+"F4.imprint","IMPRINT",FACE,{"disambiguationData":[TD([[makeQuery(id+"F4.imprint","IMPRINT",EDGE,{"derivedFrom":sQuery(id+"F4.wireOp",EDGE,"E21.sketch_text.stroke-1930")}),1.0]])]});
            var Q266;
            Q266=makeQuery(id+"F4.imprint","IMPRINT",FACE,{"disambiguationData":[TD([[makeQuery(id+"F4.imprint","IMPRINT",EDGE,{"derivedFrom":sQuery(id+"F4.wireOp",EDGE,"E21.sketch_text.stroke-1664")}),-1.0]])]});
            var Q267;
            Q267=makeQuery(id+"F4.imprint","IMPRINT",FACE,{"disambiguationData":[TD([[makeQuery(id+"F4.imprint","IMPRINT",EDGE,{"derivedFrom":sQuery(id+"F4.wireOp",EDGE,"E21.sketch_text.stroke-373")}),1.0]])]});
            var Q268;
            Q268=makeQuery(id+"F4.imprint","IMPRINT",FACE,{"disambiguationData":[TD([[makeQuery(id+"F4.imprint","IMPRINT",EDGE,{"derivedFrom":sQuery(id+"F4.wireOp",EDGE,"E21.sketch_text.stroke-130")}),1.0]])]});
            var Q269;
            Q269=makeQuery(id+"F4.imprint","IMPRINT",FACE,{"disambiguationData":[TD([[makeQuery(id+"F4.imprint","IMPRINT",EDGE,{"derivedFrom":sQuery(id+"F4.wireOp",EDGE,"E21.sketch_text.stroke-2238")}),-1.0]])]});
            var Q270;
            Q270=makeQuery(id+"F4.imprint","IMPRINT",FACE,{"disambiguationData":[TD([[makeQuery(id+"F4.imprint","IMPRINT",EDGE,{"derivedFrom":sQuery(id+"F4.wireOp",EDGE,"E20.sketch_text.stroke-1061")}),1.0]])]});
            var Q271;
            Q271=makeQuery(id+"F4.imprint","IMPRINT",FACE,{"disambiguationData":[TD([[makeQuery(id+"F4.imprint","IMPRINT",EDGE,{"derivedFrom":sQuery(id+"F4.wireOp",EDGE,"E21.sketch_text.stroke-1218")}),1.0]])]});
            var Q272;
            Q272=makeQuery(id+"F4.imprint","IMPRINT",FACE,{"disambiguationData":[TD([[makeQuery(id+"F4.imprint","IMPRINT",EDGE,{"derivedFrom":sQuery(id+"F4.wireOp",EDGE,"E21.sketch_text.stroke-658")}),1.0]])]});
            var Q273;
            Q273=makeQuery(id+"F4.imprint","IMPRINT",FACE,{"disambiguationData":[TD([[makeQuery(id+"F4.imprint","IMPRINT",EDGE,{"derivedFrom":sQuery(id+"F4.wireOp",EDGE,"E21.sketch_text.stroke-1959")}),-1.0]])]});
            var Q274;
            Q274=makeQuery(id+"F4.imprint","IMPRINT",FACE,{"disambiguationData":[TD([[makeQuery(id+"F4.imprint","IMPRINT",EDGE,{"derivedFrom":sQuery(id+"F4.wireOp",EDGE,"E21.sketch_text.stroke-405")}),1.0]])]});
            var Q275;
            Q275=makeQuery(id+"F4.imprint","IMPRINT",FACE,{"disambiguationData":[TD([[makeQuery(id+"F4.imprint","IMPRINT",EDGE,{"derivedFrom":sQuery(id+"F4.wireOp",EDGE,"E20.sketch_text.stroke-1328")}),-1.0]])]});
            var Q276;
            Q276=makeQuery(id+"F4.imprint","IMPRINT",FACE,{"disambiguationData":[TD([[makeQuery(id+"F4.imprint","IMPRINT",EDGE,{"derivedFrom":sQuery(id+"F4.wireOp",EDGE,"E21.sketch_text.stroke-1443")}),1.0]])]});
            var Q277;
            Q277=makeQuery(id+"F4.imprint","IMPRINT",FACE,{"disambiguationData":[TD([[makeQuery(id+"F4.imprint","IMPRINT",EDGE,{"derivedFrom":sQuery(id+"F4.wireOp",EDGE,"E21.sketch_text.stroke-1223")}),-1.0]])]});
            var Q278;
            Q278=makeQuery(id+"F4.imprint","IMPRINT",FACE,{"disambiguationData":[TD([[makeQuery(id+"F4.imprint","IMPRINT",EDGE,{"derivedFrom":sQuery(id+"F4.wireOp",EDGE,"E21.sketch_text.stroke-1985")}),1.0]])]});
            var Q279;
            Q279=makeQuery(id+"F4.imprint","IMPRINT",FACE,{"disambiguationData":[TD([[makeQuery(id+"F4.imprint","IMPRINT",EDGE,{"derivedFrom":sQuery(id+"F4.wireOp",EDGE,"E21.sketch_text.stroke-1711")}),-1.0]])]});
            var Q280;
            Q280=makeQuery(id+"F4.imprint","IMPRINT",FACE,{"disambiguationData":[TD([[makeQuery(id+"F4.imprint","IMPRINT",EDGE,{"derivedFrom":sQuery(id+"F4.wireOp",EDGE,"E20.sketch_text.stroke-72")}),-1.0]])]});
            var Q281;
            Q281=makeQuery(id+"F4.imprint","IMPRINT",FACE,{"disambiguationData":[TD([[makeQuery(id+"F4.imprint","IMPRINT",EDGE,{"derivedFrom":sQuery(id+"F4.wireOp",EDGE,"E20.sketch_text.stroke-76")}),-1.0]])]});
            var Q282;
            Q282=makeQuery(id+"F4.imprint","IMPRINT",FACE,{"disambiguationData":[TD([[makeQuery(id+"F4.imprint","IMPRINT",EDGE,{"derivedFrom":sQuery(id+"F4.wireOp",EDGE,"E21.sketch_text.stroke-1766")}),1.0]])]});
            var Q283;
            Q283=makeQuery(id+"F4.imprint","IMPRINT",FACE,{"disambiguationData":[TD([[makeQuery(id+"F4.imprint","IMPRINT",EDGE,{"derivedFrom":sQuery(id+"F4.wireOp",EDGE,"E21.sketch_text.stroke-1491")}),1.0]])]});
            var Q284;
            Q284=makeQuery(id+"F4.imprint","IMPRINT",FACE,{"disambiguationData":[TD([[makeQuery(id+"F4.imprint","IMPRINT",EDGE,{"derivedFrom":sQuery(id+"F4.wireOp",EDGE,"E21.sketch_text.stroke-732")}),-1.0]])]});
            var Q285;
            Q285=makeQuery(id+"F4.imprint","IMPRINT",FACE,{"disambiguationData":[TD([[makeQuery(id+"F4.imprint","IMPRINT",EDGE,{"derivedFrom":sQuery(id+"F4.wireOp",EDGE,"E21.sketch_text.stroke-456")}),1.0]])]});
            var Q286;
            Q286=makeQuery(id+"F4.imprint","IMPRINT",FACE,{"disambiguationData":[TD([[makeQuery(id+"F4.imprint","IMPRINT",EDGE,{"derivedFrom":sQuery(id+"F4.wireOp",EDGE,"E21.sketch_text.stroke-218")}),1.0]])]});
            var Q287;
            Q287=makeQuery(id+"F4.imprint","IMPRINT",FACE,{"disambiguationData":[TD([[makeQuery(id+"F4.imprint","IMPRINT",EDGE,{"derivedFrom":sQuery(id+"F4.wireOp",EDGE,"E21.sketch_text.stroke-1464")}),-1.0]])]});
            var Q288;
            Q288=makeQuery(id+"F4.imprint","IMPRINT",FACE,{"disambiguationData":[TD([[makeQuery(id+"F4.imprint","IMPRINT",EDGE,{"derivedFrom":sQuery(id+"F4.wireOp",EDGE,"E21.sketch_text.stroke-461")}),-1.0]])]});
            var Q289;
            Q289=makeQuery(id+"F4.imprint","IMPRINT",FACE,{"disambiguationData":[TD([[makeQuery(id+"F4.imprint","IMPRINT",EDGE,{"derivedFrom":sQuery(id+"F4.wireOp",EDGE,"E21.sketch_text.stroke-1016")}),-1.0]])]});
            var Q290;
            Q290=makeQuery(id+"F4.imprint","IMPRINT",FACE,{"disambiguationData":[TD([[makeQuery(id+"F4.imprint","IMPRINT",EDGE,{"derivedFrom":sQuery(id+"F4.wireOp",EDGE,"E21.sketch_text.stroke-487")}),1.0]])]});
            var Q291;
            Q291=makeQuery(id+"F4.imprint","IMPRINT",FACE,{"disambiguationData":[TD([[makeQuery(id+"F4.imprint","IMPRINT",EDGE,{"derivedFrom":sQuery(id+"F4.wireOp",EDGE,"E21.sketch_text.stroke-1543")}),1.0]])]});
            var Q292;
            Q292=makeQuery(id+"F4.imprint","IMPRINT",FACE,{"disambiguationData":[TD([[makeQuery(id+"F4.imprint","IMPRINT",EDGE,{"derivedFrom":sQuery(id+"F4.wireOp",EDGE,"E21.sketch_text.stroke-1038")}),1.0]])]});
            var Q293;
            Q293=makeQuery(id+"F4.imprint","IMPRINT",FACE,{"disambiguationData":[TD([[makeQuery(id+"F4.imprint","IMPRINT",EDGE,{"derivedFrom":sQuery(id+"F4.wireOp",EDGE,"E21.sketch_text.stroke-1277")}),-1.0]])]});
            var Q294;
            Q294=makeQuery(id+"F4.imprint","IMPRINT",FACE,{"disambiguationData":[TD([[makeQuery(id+"F4.imprint","IMPRINT",EDGE,{"derivedFrom":sQuery(id+"F4.wireOp",EDGE,"E21.sketch_text.stroke-811")}),1.0]])]});
            var Q295;
            Q295=makeQuery(id+"F4.imprint","IMPRINT",FACE,{"disambiguationData":[TD([[makeQuery(id+"F4.imprint","IMPRINT",EDGE,{"derivedFrom":sQuery(id+"F4.wireOp",EDGE,"E21.sketch_text.stroke-6")}),-1.0]])]});
            var Q296;
            Q296=makeQuery(id+"F4.imprint","IMPRINT",FACE,{"disambiguationData":[TD([[makeQuery(id+"F4.imprint","IMPRINT",EDGE,{"derivedFrom":sQuery(id+"F4.wireOp",EDGE,"E21.sketch_text.stroke-1555")}),-1.0]])]});
            var Q297;
            Q297=makeQuery(id+"F4.imprint","IMPRINT",FACE,{"disambiguationData":[TD([[makeQuery(id+"F4.imprint","IMPRINT",EDGE,{"derivedFrom":sQuery(id+"F4.wireOp",EDGE,"E21.sketch_text.stroke-1070")}),-1.0]])]});
            var Q298;
            Q298=makeQuery(id+"F4.imprint","IMPRINT",FACE,{"disambiguationData":[TD([[makeQuery(id+"F4.imprint","IMPRINT",EDGE,{"derivedFrom":sQuery(id+"F4.wireOp",EDGE,"E21.sketch_text.stroke-2153")}),1.0]])]});
            var Q299;
            Q299=makeQuery(id+"F4.imprint","IMPRINT",FACE,{"disambiguationData":[TD([[makeQuery(id+"F4.imprint","IMPRINT",EDGE,{"derivedFrom":sQuery(id+"F4.wireOp",EDGE,"E20.sketch_text.stroke-340")}),-1.0]])]});
            var Q300;
            Q300=makeQuery(id+"F4.imprint","IMPRINT",FACE,{"disambiguationData":[TD([[makeQuery(id+"F4.imprint","IMPRINT",EDGE,{"derivedFrom":sQuery(id+"F4.wireOp",EDGE,"E21.sketch_text.stroke-859")}),1.0]])]});
            var Q301;
            Q301=makeQuery(id+"F4.imprint","IMPRINT",FACE,{"disambiguationData":[TD([[makeQuery(id+"F4.imprint","IMPRINT",EDGE,{"derivedFrom":sQuery(id+"F4.wireOp",EDGE,"E21.sketch_text.stroke-573")}),1.0]])]});
            var Q302;
            Q302=makeQuery(id+"F4.imprint","IMPRINT",FACE,{"disambiguationData":[TD([[makeQuery(id+"F4.imprint","IMPRINT",EDGE,{"derivedFrom":sQuery(id+"F4.wireOp",EDGE,"E21.sketch_text.stroke-1329")}),1.0]])]});
            var Q303;
            Q303=makeQuery(id+"F4.imprint","IMPRINT",FACE,{"disambiguationData":[TD([[makeQuery(id+"F4.imprint","IMPRINT",EDGE,{"derivedFrom":sQuery(id+"F4.wireOp",EDGE,"E21.sketch_text.stroke-2244")}),-1.0]])]});
            var Q304;
            Q304=makeQuery(id+"F4.imprint","IMPRINT",FACE,{"disambiguationData":[TD([[makeQuery(id+"F4.imprint","IMPRINT",EDGE,{"derivedFrom":sQuery(id+"F4.wireOp",EDGE,"E21.sketch_text.stroke-1252")}),-1.0]])]});
            var Q305;
            Q305=makeQuery(id+"F4.imprint","IMPRINT",FACE,{"disambiguationData":[TD([[makeQuery(id+"F4.imprint","IMPRINT",EDGE,{"derivedFrom":sQuery(id+"F4.wireOp",EDGE,"E21.sketch_text.stroke-76")}),-1.0]])]});
            var Q306;
            Q306=makeQuery(id+"F4.imprint","IMPRINT",FACE,{"disambiguationData":[TD([[makeQuery(id+"F4.imprint","IMPRINT",EDGE,{"derivedFrom":sQuery(id+"F4.wireOp",EDGE,"E21.sketch_text.stroke-1227")}),-1.0]])]});
            extrude(context, id + "F5", {"entities" : qUnion([Q0, Q1, Q2, Q3, Q4, Q5, Q6, Q7, Q8, Q9, Q10, Q11, Q12, Q13, Q14, Q15, Q16, Q17, Q18, Q19, Q20, Q21, Q22, Q23, Q24, Q25, Q26, Q27, Q28, Q29, Q30, Q31, Q32, Q33, Q34, Q35, Q36, Q37, Q38, Q39, Q40, Q41, Q42, Q43, Q44, Q45, Q46, Q47, Q48, Q49, Q50, Q51, Q52, Q53, Q54, Q55, Q56, Q57, Q58, Q59, Q60, Q61, Q62, Q63, Q64, Q65, Q66, Q67, Q68, Q69, Q70, Q71, Q72, Q73, Q74, Q75, Q76, Q77, Q78, Q79, Q80, Q81, Q82, Q83, Q84, Q85, Q86, Q87, Q88, Q89, Q90, Q91, Q92, Q93, Q94, Q95, Q96, Q97, Q98, Q99, Q100, Q101, Q102, Q103, Q104, Q105, Q106, Q107, Q108, Q109, Q110, Q111, Q112, Q113, Q114, Q115, Q116, Q117, Q118, Q119, Q120, Q121, Q122, Q123, Q124, Q125, Q126, Q127, Q128, Q129, Q130, Q131, Q132, Q133, Q134, Q135, Q136, Q137, Q138, Q139, Q140, Q141, Q142, Q143, Q144, Q145, Q146, Q147, Q148, Q149, Q150, Q151, Q152, Q153, Q154, Q155, Q156, Q157, Q158, Q159, Q160, Q161, Q162, Q163, Q164, Q165, Q166, Q167, Q168, Q169, Q170, Q171, Q172, Q173, Q174, Q175, Q176, Q177, Q178, Q179, Q180, Q181, Q182, Q183, Q184, Q185, Q186, Q187, Q188, Q189, Q190, Q191, Q192, Q193, Q194, Q195, Q196, Q197, Q198, Q199, Q200, Q201, Q202, Q203, Q204, Q205, Q206, Q207, Q208, Q209, Q210, Q211, Q212, Q213, Q214, Q215, Q216, Q217, Q218, Q219, Q220, Q221, Q222, Q223, Q224, Q225, Q226, Q227, Q228, Q229, Q230, Q231, Q232, Q233, Q234, Q235, Q236, Q237, Q238, Q239, Q240, Q241, Q242, Q243, Q244, Q245, Q246, Q247, Q248, Q249, Q250, Q251, Q252, Q253, Q254, Q255, Q256, Q257, Q258, Q259, Q260, Q261, Q262, Q263, Q264, Q265, Q266, Q267, Q268, Q269, Q270, Q271, Q272, Q273, Q274, Q275, Q276, Q277, Q278, Q279, Q280, Q281, Q282, Q283, Q284, Q285, Q286, Q287, Q288, Q289, Q290, Q291, Q292, Q293, Q294, Q295, Q296, Q297, Q298, Q299, Q300, Q301, Q302, Q303, Q304, Q305, Q306]), "operationType" : NewBodyOperationType.REMOVE, "oppositeDirection" : true, "depth" : 2.54 * mm, "offsetDistance" : 25.4 * mm});
        }
    });
